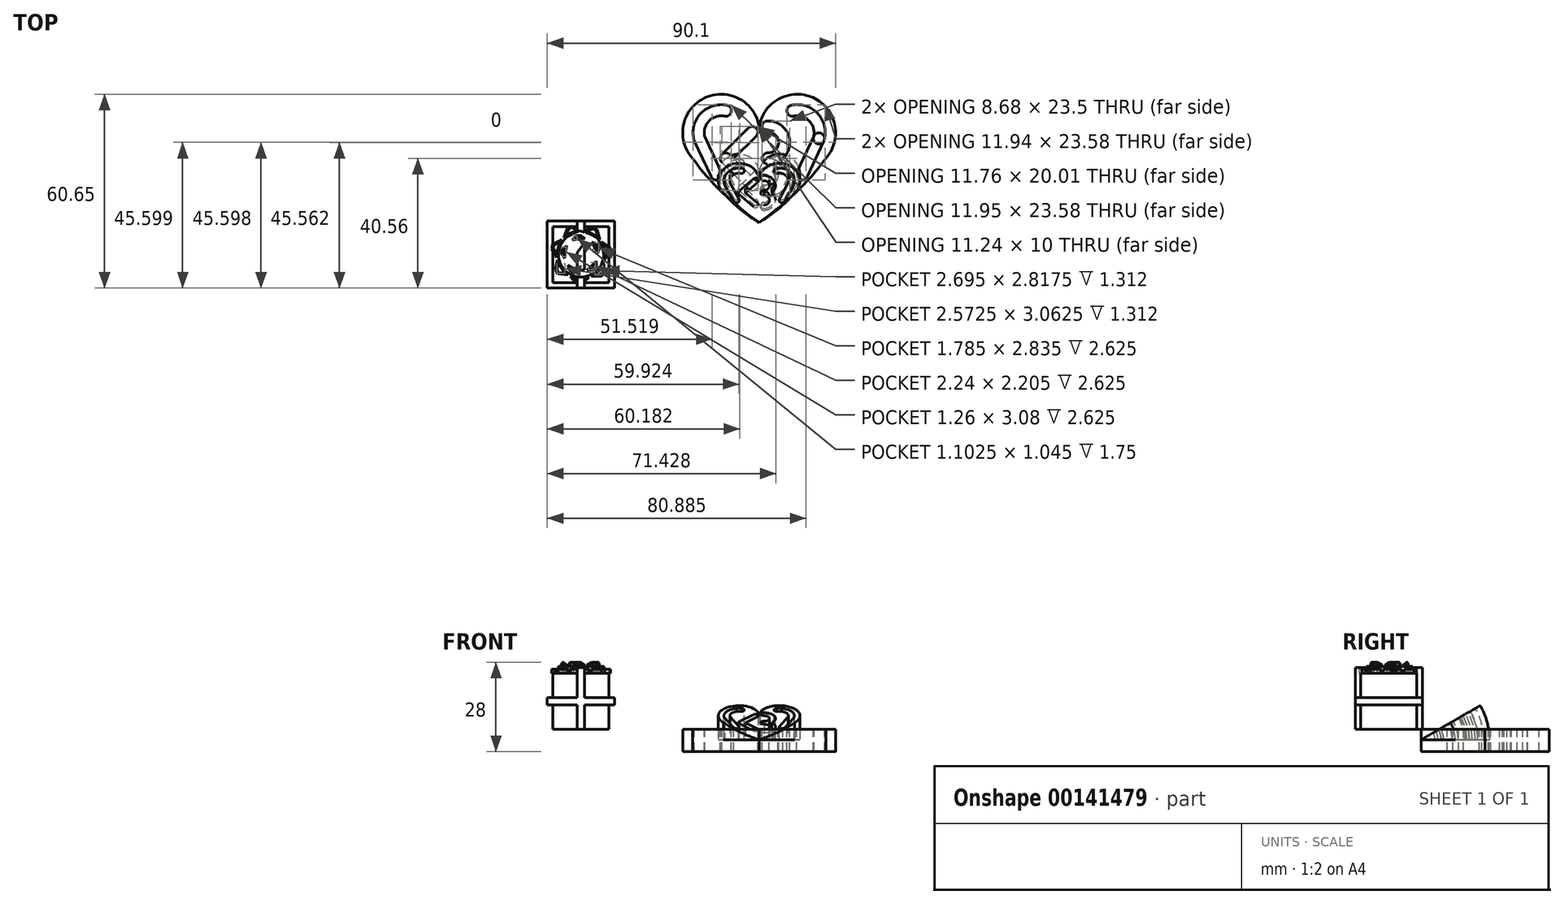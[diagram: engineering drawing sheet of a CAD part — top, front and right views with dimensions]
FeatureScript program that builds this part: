
annotation { "Feature Type Name" : "Feature", "Feature Type Description" : "" }
export const myFeature = defineFeature(function(context is Context, id is Id, definition is map)
    precondition{}
    {
        {
            var Q0;
            Q0=qCreatedBy(makeId("Top.planeOp"),FACE);
            var sketch = newSketch(context, id + "F0", { "sketchPlane" : qUnion([Q0])});
            skPoint(sketch, "E0", {"position": v(20.81, 20) * mm});
            skPoint(sketch, "E0.positionSnap0", {"position": v(0, 20) * mm});
            skPoint(sketch, "E0.positionSnap1", {"position": v(20.81, 40) * mm});
            skPoint(sketch, "E1", {"position": v(20.81, 30) * mm});
            skPoint(sketch, "E2", {"position": v(41.62, 20) * mm});
            skPoint(sketch, "E3", {"position": v(0, 30) * mm});
            skPoint(sketch, "E4", {"position": v(41.62, 30) * mm});
            skPoint(sketch, "E5", {"position": v(10.4, 40) * mm});
            skPoint(sketch, "E6", {"position": v(30.21, 39.83) * mm});
            skArc(sketch, "E7", {"start": v(20.81, 30) * mm, "mid": v(3.73, 38.9) * mm, "end": v(0, 20) * mm});
            skArc(sketch, "E8", {"start": v(0, 20) * mm, "mid": v(9.56, 9.12) * mm, "end": v(20.81, 0) * mm});
            skLineSegment(sketch, "E9.MirrorCS", {"start": v(20.81, 30) * mm, "end": v(20.81, 30) * mm});
            skArc(sketch, "E10.MirrorCS", {"start": v(41.62, 20) * mm, "mid": v(32.06, 9.12) * mm, "end": v(20.81, 0) * mm});
            skLineSegment(sketch, "E11.bottom", {"start": v(10.4, 30) * mm, "end": v(15.6, 30) * mm, "construction": true});
            skLineSegment(sketch, "E11.top", {"start": v(10.4, 10) * mm, "end": v(31.22, 10) * mm, "construction": true});
            skLineSegment(sketch, "E11.left", {"start": v(10.4, 30) * mm, "end": v(10.4, 20) * mm, "construction": true});
            skLineSegment(sketch, "E11.right", {"start": v(31.22, 30) * mm, "end": v(31.22, 20) * mm, "construction": true});
            skLineSegment(sketch, "E12", {"start": v(0, 20) * mm, "end": v(10.4, 20) * mm, "construction": true});
            skLineSegment(sketch, "E13", {"start": v(20.81, 30) * mm, "end": v(31.22, 30) * mm, "construction": true});
            skPoint(sketch, "E14", {"position": v(15.6, 30) * mm});
            skPoint(sketch, "E15", {"position": v(10.4, 20) * mm});
            skLineSegment(sketch, "E16", {"start": v(10.4, 20) * mm, "end": v(10.4, 10) * mm, "construction": true});
            skLineSegment(sketch, "E17", {"start": v(10.4, 20) * mm, "end": v(20.94, 20) * mm, "construction": true});
            skLineSegment(sketch, "E18", {"start": v(15.6, 30) * mm, "end": v(20.81, 30) * mm, "construction": true});
            skPoint(sketch, "E19", {"position": v(5.2, 20) * mm});
            skPoint(sketch, "E20", {"position": v(26.01, 30) * mm});
            skPoint(sketch, "E21", {"position": v(26.01, 20) * mm});
            skPoint(sketch, "E22", {"position": v(31.22, 20) * mm});
            skLineSegment(sketch, "E23", {"start": v(31.22, 20) * mm, "end": v(31.22, 15) * mm, "construction": true});
            skPoint(sketch, "E24", {"position": v(31.22, 25) * mm});
            skArc(sketch, "E25", {"start": v(23.45, 20) * mm, "mid": v(28.65, 25) * mm, "end": v(23.45, 30) * mm});
            skArc(sketch, "E26.MirrorCS", {"start": v(23.45, 20) * mm, "mid": v(28.65, 15) * mm, "end": v(23.45, 10) * mm});
            skLineSegment(sketch, "E27", {"start": v(20.94, 20) * mm, "end": v(26.01, 20) * mm, "construction": true});
            skLineSegment(sketch, "E28", {"start": v(26.01, 20) * mm, "end": v(41.62, 20) * mm, "construction": true});
            skPoint(sketch, "E29", {"position": v(23.48, 20) * mm});
            skPoint(sketch, "E30", {"position": v(18.21, 30) * mm});
            skArc(sketch, "E31.1.startCap", {"start": v(23.38, 18.25) * mm, "mid": v(21.7, 20.07) * mm, "end": v(23.52, 21.75) * mm});
            skArc(sketch, "E31.1.endCap", {"start": v(23.52, 28.25) * mm, "mid": v(21.7, 29.93) * mm, "end": v(23.38, 31.75) * mm});
            skArc(sketch, "E31.1.left", {"start": v(23.52, 21.75) * mm, "mid": v(26.9, 25) * mm, "end": v(23.52, 28.25) * mm});
            skArc(sketch, "E31.1.right", {"start": v(23.38, 18.25) * mm, "mid": v(30.4, 25) * mm, "end": v(23.38, 31.75) * mm});
            skArc(sketch, "E31.2.startCap", {"start": v(23.52, 18.25) * mm, "mid": v(21.7, 19.93) * mm, "end": v(23.38, 21.75) * mm});
            skArc(sketch, "E31.2.endCap", {"start": v(23.38, 8.25) * mm, "mid": v(21.7, 10.07) * mm, "end": v(23.52, 11.75) * mm});
            skArc(sketch, "E31.2.left", {"start": v(23.38, 21.75) * mm, "mid": v(30.4, 15) * mm, "end": v(23.38, 8.25) * mm});
            skArc(sketch, "E31.2.right", {"start": v(23.52, 18.25) * mm, "mid": v(26.9, 15) * mm, "end": v(23.52, 11.75) * mm});
            skLineSegment(sketch, "E32", {"start": v(0, 0) * mm, "end": v(75.27, 0) * mm, "construction": true});
            skPoint(sketch, "E33", {"position": v(20.81, 10) * mm});
            skPoint(sketch, "E34", {"position": v(20.81, 5) * mm});
            skPoint(sketch, "E35", {"position": v(17.47, 5) * mm});
            skPoint(sketch, "E36", {"position": v(24.15, 5) * mm});
            skLineSegment(sketch, "E37", {"start": v(17.47, 5) * mm, "end": v(24.15, 5) * mm, "construction": true});
            skArc(sketch, "E38", {"start": v(20.81, 30) * mm, "mid": v(23.99, 36.37) * mm, "end": v(30.21, 39.83) * mm});
            skArc(sketch, "E39", {"start": v(30.21, 39.83) * mm, "mid": v(41.4, 36.35) * mm, "end": v(44.32, 25) * mm});
            skLineSegment(sketch, "E40", {"start": v(31.22, 25) * mm, "end": v(46.35, 25) * mm, "construction": true});
            skArc(sketch, "E41", {"start": v(44.32, 25) * mm, "mid": v(43.27, 22.34) * mm, "end": v(41.62, 20) * mm});
            skArc(sketch, "E42.0", {"start": v(31.24, 34.94) * mm, "mid": v(37.78, 32.9) * mm, "end": v(39.49, 26.27) * mm});
            skLineSegment(sketch, "E43", {"start": v(31.22, 15) * mm, "end": v(31.22, 10) * mm, "construction": true});
            skLineSegment(sketch, "E44", {"start": v(39.49, 26.27) * mm, "end": v(34.24, 15) * mm});
            skArc(sketch, "E45.0.startCap", {"start": v(31.6, 33.23) * mm, "mid": v(29.53, 34.58) * mm, "end": v(30.88, 36.65) * mm});
            skArc(sketch, "E45.0.endCap", {"start": v(41.18, 25.83) * mm, "mid": v(39.04, 24.58) * mm, "end": v(37.8, 26.72) * mm});
            skArc(sketch, "E45.0.left", {"start": v(30.88, 36.65) * mm, "mid": v(39.05, 34.11) * mm, "end": v(41.18, 25.83) * mm});
            skArc(sketch, "E45.0.right", {"start": v(31.6, 33.23) * mm, "mid": v(36.51, 31.7) * mm, "end": v(37.8, 26.72) * mm});
            skArc(sketch, "E45.1.startCap", {"start": v(37.9, 27) * mm, "mid": v(40.23, 27.86) * mm, "end": v(41.08, 25.53) * mm});
            skArc(sketch, "E45.1.endCap", {"start": v(35.83, 14.26) * mm, "mid": v(33.5, 13.41) * mm, "end": v(32.66, 15.74) * mm});
            skLineSegment(sketch, "E45.1.left", {"start": v(41.08, 25.53) * mm, "end": v(35.83, 14.26) * mm});
            skLineSegment(sketch, "E45.1.right", {"start": v(37.9, 27) * mm, "end": v(32.66, 15.74) * mm});
            skLineSegment(sketch, "E46", {"start": v(20.81, 30) * mm, "end": v(20.81, 0) * mm, "construction": true});
            skLineSegment(sketch, "E47.MirrorCS", {"start": v(3.72, 27) * mm, "end": v(8.97, 15.74) * mm});
            skLineSegment(sketch, "E48.MirrorCS", {"start": v(2.13, 26.27) * mm, "end": v(7.38, 15) * mm});
            skArc(sketch, "E49.MirrorCS", {"start": v(5.8, 14.26) * mm, "mid": v(8.12, 13.41) * mm, "end": v(8.97, 15.74) * mm});
            skLineSegment(sketch, "E50.MirrorCS", {"start": v(0.55, 25.53) * mm, "end": v(5.8, 14.26) * mm});
            skArc(sketch, "E51.MirrorCS", {"start": v(3.72, 27) * mm, "mid": v(1.4, 27.86) * mm, "end": v(0.55, 25.53) * mm});
            skArc(sketch, "E52.MirrorCS", {"start": v(0.44, 25.83) * mm, "mid": v(2.58, 24.58) * mm, "end": v(3.83, 26.72) * mm});
            skArc(sketch, "E53.MirrorCS", {"start": v(10.74, 36.65) * mm, "mid": v(2.57, 34.11) * mm, "end": v(0.44, 25.83) * mm});
            skArc(sketch, "E54.MirrorCS", {"start": v(10.38, 34.94) * mm, "mid": v(3.84, 32.9) * mm, "end": v(2.13, 26.27) * mm});
            skArc(sketch, "E55.MirrorCS", {"start": v(10.02, 33.23) * mm, "mid": v(5.1, 31.7) * mm, "end": v(3.83, 26.72) * mm});
            skArc(sketch, "E56.MirrorCS", {"start": v(10.02, 33.23) * mm, "mid": v(12.1, 34.58) * mm, "end": v(10.74, 36.65) * mm});
            skLineSegment(sketch, "E57", {"start": v(10.4, 20) * mm, "end": v(18.66, 28.25) * mm});
            skLineSegment(sketch, "E58.MirrorCS", {"start": v(10.4, 20) * mm, "end": v(18.66, 11.75) * mm});
            skArc(sketch, "E59.0.startCap", {"start": v(11.64, 18.76) * mm, "mid": v(9.17, 18.76) * mm, "end": v(9.17, 21.24) * mm});
            skArc(sketch, "E59.0.endCap", {"start": v(17.42, 29.49) * mm, "mid": v(19.9, 29.49) * mm, "end": v(19.9, 27.01) * mm});
            skLineSegment(sketch, "E59.0.left", {"start": v(9.17, 21.24) * mm, "end": v(17.42, 29.49) * mm});
            skLineSegment(sketch, "E59.0.right", {"start": v(11.64, 18.76) * mm, "end": v(19.9, 27.01) * mm});
            skArc(sketch, "E59.1.startCap", {"start": v(9.17, 18.76) * mm, "mid": v(9.17, 21.24) * mm, "end": v(11.64, 21.24) * mm});
            skArc(sketch, "E59.1.endCap", {"start": v(19.9, 12.99) * mm, "mid": v(19.9, 10.51) * mm, "end": v(17.42, 10.51) * mm});
            skLineSegment(sketch, "E59.1.left", {"start": v(11.64, 21.24) * mm, "end": v(19.9, 12.99) * mm});
            skLineSegment(sketch, "E59.1.right", {"start": v(9.17, 18.76) * mm, "end": v(17.42, 10.51) * mm});
            skSolve(sketch);
        }
        {
            var Q0;
            Q0=makeQuery(id+"F0.imprint","IMPRINT",FACE,{"disambiguationData":[TD([[makeQuery(id+"F0.imprint","IMPRINT",EDGE,{"derivedFrom":sQuery(id+"F0.wireOp",EDGE,"E7")}),1.0]])]});
            var Q1;
            Q1=sQuery(id+"F0.wireOp",EDGE,"E32");
            revolve(context, id + "F1", {"entities" : qUnion([Q0]), "axis" : qUnion([Q1]), "revolveType" : RevolveType.ONE_DIRECTION, "angle" : (PI / 6) * radian});
        }
        {
            var Q0;
            Q0=makeQuery(id+"F1.opRevolve","CAP_FACE",FACE,{"disambiguationData":[OSD([sQuery(id+"F0.wireOp",EDGE,"E7"),sQuery(id+"F0.wireOp",EDGE,"E8"),sQuery(id+"F0.wireOp",EDGE,"E10.MirrorCS"),sQuery(id+"F0.wireOp",EDGE,"E31.1.endCap"),sQuery(id+"F0.wireOp",EDGE,"E31.1.left"),sQuery(id+"F0.wireOp",EDGE,"E31.1.right"),sQuery(id+"F0.wireOp",EDGE,"E31.2.startCap"),sQuery(id+"F0.wireOp",EDGE,"E31.2.endCap"),sQuery(id+"F0.wireOp",EDGE,"E31.2.left"),sQuery(id+"F0.wireOp",EDGE,"E31.2.right"),sQuery(id+"F0.wireOp",EDGE,"E38"),sQuery(id+"F0.wireOp",EDGE,"E39"),sQuery(id+"F0.wireOp",EDGE,"E41"),sQuery(id+"F0.wireOp",EDGE,"E45.0.startCap"),sQuery(id+"F0.wireOp",EDGE,"E45.0.left"),sQuery(id+"F0.wireOp",EDGE,"E45.0.right"),sQuery(id+"F0.wireOp",EDGE,"E45.1.startCap"),sQuery(id+"F0.wireOp",EDGE,"E45.1.endCap"),sQuery(id+"F0.wireOp",EDGE,"E45.1.left"),sQuery(id+"F0.wireOp",EDGE,"E45.1.right"),sQuery(id+"F0.wireOp",EDGE,"E47.MirrorCS"),sQuery(id+"F0.wireOp",EDGE,"E49.MirrorCS"),sQuery(id+"F0.wireOp",EDGE,"E50.MirrorCS"),sQuery(id+"F0.wireOp",EDGE,"E52.MirrorCS"),sQuery(id+"F0.wireOp",EDGE,"E53.MirrorCS"),sQuery(id+"F0.wireOp",EDGE,"E55.MirrorCS"),sQuery(id+"F0.wireOp",EDGE,"E56.MirrorCS"),sQuery(id+"F0.wireOp",EDGE,"E59.0.endCap"),sQuery(id+"F0.wireOp",EDGE,"E59.0.left"),sQuery(id+"F0.wireOp",EDGE,"E59.0.right"),sQuery(id+"F0.wireOp",EDGE,"E59.1.startCap"),sQuery(id+"F0.wireOp",EDGE,"E59.1.endCap"),sQuery(id+"F0.wireOp",EDGE,"E59.1.left"),sQuery(id+"F0.wireOp",EDGE,"E59.1.right")])],"isStart":true});
            var Q1;
            {var subQ0=sQuery(id+"F0.wireOp",EDGE,"E53.MirrorCS");Q1=makeQuery(id+"F0.imprint","IMPRINT",FACE,{"disambiguationData":[TD([[makeQuery(id+"F0.imprint","IMPRINT",EDGE,{"derivedFrom":subQ0}),1.0]])]});}
            var Q2;
            {var subQ3=sQuery(id+"F0.wireOp",EDGE,"E49.MirrorCS");Q2=makeQuery(id+"F0.imprint","IMPRINT",FACE,{"disambiguationData":[TD([[makeQuery(id+"F0.imprint","IMPRINT",EDGE,{"derivedFrom":subQ3}),1.0]])]});}
            var Q3;
            {var subQ2=sQuery(id+"F0.wireOp",EDGE,"E48.MirrorCS");var subQ6=sQuery(id+"F0.wireOp",EDGE,"E54.MirrorCS");var subQ8=makeQuery(id+"F0.imprint","INTERSECT",VERTEX,{"derivedFrom":[subQ2,subQ6]});Q3=makeQuery(id+"F0.imprint","IMPRINT",FACE,{"disambiguationData":[TD([[makeQuery(id+"F0.imprint","IMPRINT",EDGE,{"disambiguationData":[TD([[subQ8,-1.0]])],"derivedFrom":subQ2}),-1.0]])]});}
            var Q4;
            {var subQ0=sQuery(id+"F0.wireOp",EDGE,"E45.1.endCap");Q4=makeQuery(id+"F0.imprint","IMPRINT",FACE,{"disambiguationData":[TD([[makeQuery(id+"F0.imprint","IMPRINT",EDGE,{"derivedFrom":subQ0}),-1.0]])]});}
            var Q5;
            {var subQ2=sQuery(id+"F0.wireOp",EDGE,"E42.0");var subQ6=sQuery(id+"F0.wireOp",EDGE,"E44");var subQ8=makeQuery(id+"F0.imprint","INTERSECT",VERTEX,{"derivedFrom":[subQ2,subQ6]});Q5=makeQuery(id+"F0.imprint","IMPRINT",FACE,{"disambiguationData":[TD([[makeQuery(id+"F0.imprint","IMPRINT",EDGE,{"disambiguationData":[TD([[subQ8,1.0]])],"derivedFrom":subQ2}),1.0]])]});}
            var Q6;
            {var subQ5=sQuery(id+"F0.wireOp",EDGE,"E45.0.startCap");Q6=makeQuery(id+"F0.imprint","IMPRINT",FACE,{"disambiguationData":[TD([[makeQuery(id+"F0.imprint","IMPRINT",EDGE,{"derivedFrom":subQ5}),-1.0]])]});}
            var Q7;
            {var subQ5=sQuery(id+"F0.wireOp",EDGE,"E44");var subQ7=sQuery(id+"F0.wireOp",EDGE,"E42.0");var subQ8=makeQuery(id+"F0.imprint","INTERSECT",VERTEX,{"derivedFrom":[subQ7,subQ5]});Q7=makeQuery(id+"F0.imprint","IMPRINT",FACE,{"disambiguationData":[TD([[makeQuery(id+"F0.imprint","IMPRINT",EDGE,{"disambiguationData":[TD([[subQ8,1.0]])],"derivedFrom":subQ7}),-1.0]])]});}
            var Q8;
            {var subQ7=sQuery(id+"F0.wireOp",EDGE,"E47.MirrorCS");var subQ9=sQuery(id+"F0.wireOp",EDGE,"E51.MirrorCS");var subQ10=makeQuery(id+"F0.imprint","INTERSECT",VERTEX,{"derivedFrom":[subQ7,subQ9]});Q8=makeQuery(id+"F0.imprint","IMPRINT",FACE,{"disambiguationData":[TD([[makeQuery(id+"F0.imprint","IMPRINT",EDGE,{"disambiguationData":[TD([[subQ10,-1.0]])],"derivedFrom":subQ7}),-1.0]])]});}
            var Q9;
            {var subQ0=sQuery(id+"F0.wireOp",EDGE,"E58.MirrorCS");var subQ1=sQuery(id+"F0.wireOp",EDGE,"E57");var subQ2=makeQuery(id+"F0.imprint","INTERSECT",VERTEX,{"derivedFrom":[subQ1,subQ0]});Q9=makeQuery(id+"F0.imprint","IMPRINT",FACE,{"disambiguationData":[TD([[makeQuery(id+"F0.imprint","IMPRINT",EDGE,{"disambiguationData":[TD([[subQ2,-1.0]])],"derivedFrom":subQ1}),-1.0]])]});}
            var Q10;
            {var subQ1=sQuery(id+"F0.wireOp",EDGE,"E59.0.startCap");Q10=makeQuery(id+"F0.imprint","IMPRINT",FACE,{"disambiguationData":[TD([[makeQuery(id+"F0.imprint","IMPRINT",EDGE,{"derivedFrom":subQ1}),-1.0]])]});}
            var Q11;
            {var subQ1=sQuery(id+"F0.wireOp",EDGE,"E59.0.endCap");Q11=makeQuery(id+"F0.imprint","IMPRINT",FACE,{"disambiguationData":[TD([[makeQuery(id+"F0.imprint","IMPRINT",EDGE,{"derivedFrom":subQ1}),-1.0]])]});}
            var Q12;
            {var subQ4=sQuery(id+"F0.wireOp",EDGE,"E59.0.startCap");Q12=makeQuery(id+"F0.imprint","IMPRINT",FACE,{"disambiguationData":[TD([[makeQuery(id+"F0.imprint","IMPRINT",EDGE,{"derivedFrom":subQ4}),1.0]])]});}
            var Q13;
            {var subQ1=sQuery(id+"F0.wireOp",EDGE,"E31.2.endCap");Q13=makeQuery(id+"F0.imprint","IMPRINT",FACE,{"disambiguationData":[TD([[makeQuery(id+"F0.imprint","IMPRINT",EDGE,{"derivedFrom":subQ1}),-1.0]])]});}
            var Q14;
            {var subQ4=sQuery(id+"F0.wireOp",EDGE,"E31.1.endCap");Q14=makeQuery(id+"F0.imprint","IMPRINT",FACE,{"disambiguationData":[TD([[makeQuery(id+"F0.imprint","IMPRINT",EDGE,{"derivedFrom":subQ4}),-1.0]])]});}
            var Q15;
            {var subQ0=sQuery(id+"F0.wireOp",EDGE,"E26.MirrorCS");var subQ1=sQuery(id+"F0.wireOp",EDGE,"E25");var subQ2=makeQuery(id+"F0.imprint","INTERSECT",VERTEX,{"disambiguationData":[OD(1.0)],"derivedFrom":[subQ1,subQ0]});Q15=makeQuery(id+"F0.imprint","IMPRINT",FACE,{"disambiguationData":[TD([[makeQuery(id+"F0.imprint","IMPRINT",EDGE,{"disambiguationData":[TD([[subQ2,-1.0]])],"derivedFrom":subQ1}),-1.0]])]});}
            var Q16;
            {var subQ10=sQuery(id+"F0.wireOp",EDGE,"E31.1.startCap");Q16=makeQuery(id+"F0.imprint","IMPRINT",FACE,{"disambiguationData":[TD([[makeQuery(id+"F0.imprint","IMPRINT",EDGE,{"derivedFrom":subQ10}),-1.0]])]});}
            extrude(context, id + "F2", {"entities" : qUnion([Q0, Q1, Q2, Q3, Q4, Q5, Q6, Q7, Q8, Q9, Q10, Q11, Q12, Q13, Q14, Q15, Q16]), "operationType" : NewBodyOperationType.ADD, "depth" : 7 * mm});
        }
        {
            var Q0;
            Q0=makeQuery(id+"F1.opRevolve","SWEPT_BODY",BODY,{"disambiguationData":[OSD([sQuery(id+"F0.wireOp",EDGE,"E7"),sQuery(id+"F0.wireOp",EDGE,"E8"),sQuery(id+"F0.wireOp",EDGE,"E10.MirrorCS"),sQuery(id+"F0.wireOp",EDGE,"E31.1.endCap"),sQuery(id+"F0.wireOp",EDGE,"E31.1.left"),sQuery(id+"F0.wireOp",EDGE,"E31.1.right"),sQuery(id+"F0.wireOp",EDGE,"E31.2.startCap"),sQuery(id+"F0.wireOp",EDGE,"E31.2.endCap"),sQuery(id+"F0.wireOp",EDGE,"E31.2.left"),sQuery(id+"F0.wireOp",EDGE,"E31.2.right"),sQuery(id+"F0.wireOp",EDGE,"E38"),sQuery(id+"F0.wireOp",EDGE,"E39"),sQuery(id+"F0.wireOp",EDGE,"E41"),sQuery(id+"F0.wireOp",EDGE,"E45.0.startCap"),sQuery(id+"F0.wireOp",EDGE,"E45.0.left"),sQuery(id+"F0.wireOp",EDGE,"E45.0.right"),sQuery(id+"F0.wireOp",EDGE,"E45.1.startCap"),sQuery(id+"F0.wireOp",EDGE,"E45.1.endCap"),sQuery(id+"F0.wireOp",EDGE,"E45.1.left"),sQuery(id+"F0.wireOp",EDGE,"E45.1.right"),sQuery(id+"F0.wireOp",EDGE,"E47.MirrorCS"),sQuery(id+"F0.wireOp",EDGE,"E49.MirrorCS"),sQuery(id+"F0.wireOp",EDGE,"E50.MirrorCS"),sQuery(id+"F0.wireOp",EDGE,"E52.MirrorCS"),sQuery(id+"F0.wireOp",EDGE,"E53.MirrorCS"),sQuery(id+"F0.wireOp",EDGE,"E55.MirrorCS"),sQuery(id+"F0.wireOp",EDGE,"E56.MirrorCS"),sQuery(id+"F0.wireOp",EDGE,"E59.0.endCap"),sQuery(id+"F0.wireOp",EDGE,"E59.0.left"),sQuery(id+"F0.wireOp",EDGE,"E59.0.right"),sQuery(id+"F0.wireOp",EDGE,"E59.1.startCap"),sQuery(id+"F0.wireOp",EDGE,"E59.1.endCap"),sQuery(id+"F0.wireOp",EDGE,"E59.1.left"),sQuery(id+"F0.wireOp",EDGE,"E59.1.right")])]});
            var Q1;
            Q1=makeQuery(id+"F2.opExtrude","CAP_VERTEX",VERTEX,{"disambiguationData":[OSD([sQuery(id+"F0.wireOp",EDGE,"E8"),sQuery(id+"F0.wireOp",EDGE,"E10.MirrorCS")])],"isStart":false});
            transform(context, id + "F3", {"entities" : qUnion([Q0]), "transformType" : TransformType.SCALE_UNIFORMLY, "scale" : 1 / 3, "scalePoint" : qUnion([Q1]), "makeCopy" : false});
        }
        {
            var Q0;
            Q0=qCreatedBy(makeId("Top.planeOp"),FACE);
            var sketch = newSketch(context, id + "F4", { "sketchPlane" : qUnion([Q0])});
            skLineSegment(sketch, "E60.bottom", {"start": v(-43.64, -8.81) * mm, "end": v(-33.64, -8.81) * mm});
            skLineSegment(sketch, "E60.top", {"start": v(-43.64, -18.81) * mm, "end": v(-33.64, -18.81) * mm});
            skLineSegment(sketch, "E60.left", {"start": v(-43.64, -8.81) * mm, "end": v(-43.64, -18.81) * mm});
            skLineSegment(sketch, "E60.right", {"start": v(-33.64, -8.81) * mm, "end": v(-33.64, -18.81) * mm});
            skSolve(sketch);
        }
        {
            var Q0;
            Q0=makeQuery(id+"F4.imprint","IMPRINT",FACE,{"disambiguationData":[TD([[makeQuery(id+"F4.imprint","IMPRINT",EDGE,{"derivedFrom":sQuery(id+"F4.wireOp",EDGE,"E60.bottom")}),-1.0]])]});
            extrude(context, id + "F5", {"entities" : qUnion([Q0]), "depth" : 10 * mm});
        }
        {
            var Q0;
            Q0=makeQuery(id+"F5.opExtrude","SWEPT_FACE",FACE,{"disambiguationData":[OSD([sQuery(id+"F4.wireOp",EDGE,"E60.top")])]});
            var sketch = newSketch(context, id + "F6", { "sketchPlane" : qUnion([Q0])});
            skPoint(sketch, "E61", {"position": v(-43.64, 5) * mm});
            skPoint(sketch, "E62", {"position": v(-38.64, 10) * mm});
            skLineSegment(sketch, "E63", {"start": v(-43.64, 10) * mm, "end": v(-33.64, 10) * mm, "construction": true});
            skLineSegment(sketch, "E64", {"start": v(-43.64, 10) * mm, "end": v(-43.64, 0) * mm, "construction": true});
            skPoint(sketch, "E65", {"position": v(-43.64, 5.67) * mm});
            skLineSegment(sketch, "E66", {"start": v(-43.64, 5) * mm, "end": v(-33.64, 5) * mm, "construction": true});
            skLineSegment(sketch, "E67", {"start": v(-38.64, 10) * mm, "end": v(-38.64, 0) * mm, "construction": true});
            skLineSegment(sketch, "E68", {"start": v(-43.64, 5.67) * mm, "end": v(-33.64, 5.67) * mm});
            skLineSegment(sketch, "E69.MirrorCS", {"start": v(-43.64, 4.33) * mm, "end": v(-33.64, 4.33) * mm});
            skLineSegment(sketch, "E70", {"start": v(-39.31, 10) * mm, "end": v(-39.31, 0) * mm});
            skLineSegment(sketch, "E71.MirrorCS", {"start": v(-37.98, 10) * mm, "end": v(-37.98, 0) * mm});
            skSolve(sketch);
        }
        {
            var Q0;
            Q0 = qSketchRegion(id + "F6", true);
            var Q1;
            {var subQ0=sQuery(id+"F6.wireOp",EDGE,"E70");var subQ1=sQuery(id+"F6.wireOp",EDGE,"E68");var subQ2=makeQuery(id+"F6.imprint","INTERSECT",VERTEX,{"derivedFrom":[subQ1,subQ0]});Q1=makeQuery(id+"F6.imprint","IMPRINT",FACE,{"disambiguationData":[TD([[makeQuery(id+"F6.imprint","IMPRINT",EDGE,{"disambiguationData":[TD([[subQ2,-1.0]])],"derivedFrom":subQ1}),1.0]])]});}
            var Q2;
            {var subQ0=sQuery(id+"F6.wireOp",EDGE,"E68");var subQ3=sQuery(id+"F6.wireOp",EDGE,"E70");var subQ4=makeQuery(id+"F6.imprint","INTERSECT",VERTEX,{"derivedFrom":[subQ0,subQ3]});Q2=makeQuery(id+"F6.imprint","IMPRINT",FACE,{"disambiguationData":[TD([[makeQuery(id+"F6.imprint","IMPRINT",EDGE,{"disambiguationData":[TD([[subQ4,-1.0]])],"derivedFrom":subQ3}),-1.0]])]});}
            var Q3;
            {var subQ0=sQuery(id+"F6.wireOp",EDGE,"E68");var subQ3=sQuery(id+"F6.wireOp",EDGE,"E71.MirrorCS");var subQ4=makeQuery(id+"F6.imprint","INTERSECT",VERTEX,{"derivedFrom":[subQ0,subQ3]});Q3=makeQuery(id+"F6.imprint","IMPRINT",FACE,{"disambiguationData":[TD([[makeQuery(id+"F6.imprint","IMPRINT",EDGE,{"disambiguationData":[TD([[subQ4,-1.0]])],"derivedFrom":subQ3}),1.0]])]});}
            var Q4;
            {var subQ0=sQuery(id+"F6.wireOp",EDGE,"E70");var subQ1=sQuery(id+"F6.wireOp",EDGE,"E69.MirrorCS");var subQ2=makeQuery(id+"F6.imprint","INTERSECT",VERTEX,{"derivedFrom":[subQ1,subQ0]});Q4=makeQuery(id+"F6.imprint","IMPRINT",FACE,{"disambiguationData":[TD([[makeQuery(id+"F6.imprint","IMPRINT",EDGE,{"disambiguationData":[TD([[subQ2,-1.0]])],"derivedFrom":subQ1}),-1.0]])]});}
            extrude(context, id + "F7", {"entities" : qUnion([Q0, Q1, Q2, Q3, Q4]), "operationType" : NewBodyOperationType.ADD, "depth" : 1 * mm});
        }
        {
            var Q0;
            {var subQ0=sQuery(id+"F4.wireOp",EDGE,"E60.left");Q0=makeQuery(id+"F7.boolean.opBoolean","MERGE",FACE,{"derivedFrom":[makeQuery(id+"F5.opExtrude","SWEPT_FACE",FACE,{"disambiguationData":[OSD([subQ0])]}),makeQuery(id+"F7.opExtrude","SWEPT_FACE",FACE,{"disambiguationData":[OSD([sQuery(id+"F4.wireOp",EDGE,"E60.top"),subQ0])]})]});}
            var sketch = newSketch(context, id + "F8", { "sketchPlane" : qUnion([Q0])});
            skLineSegment(sketch, "E72", {"start": v(19.81, 4.33) * mm, "end": v(8.81, 4.33) * mm});
            skLineSegment(sketch, "E73", {"start": v(19.81, 5.67) * mm, "end": v(8.81, 5.67) * mm});
            skSolve(sketch);
        }
        {
            var Q0;
            {var subQ1=sQuery(id+"F4.wireOp",EDGE,"E60.left");var subQ2=sQuery(id+"F4.wireOp",EDGE,"E60.top");var subQ3=makeQuery(id+"F7.opExtrude","CAP_EDGE",EDGE,{"disambiguationData":[OSD([subQ2,subQ1])],"isStart":false});Q0=makeQuery(id+"F8.imprint","IMPRINT",FACE,{"disambiguationData":[TD([[makeQuery(id+"F8.imprint","IMPRINT",EDGE,{"derivedFrom":subQ3}),-1.0]])]});}
            extrude(context, id + "F9", {"entities" : qUnion([Q0]), "operationType" : NewBodyOperationType.ADD, "depth" : 1 * mm});
        }
        {
            var Q0;
            {var subQ0=sQuery(id+"F4.wireOp",EDGE,"E60.right");Q0=makeQuery(id+"F7.boolean.opBoolean","MERGE",FACE,{"derivedFrom":[makeQuery(id+"F5.opExtrude","SWEPT_FACE",FACE,{"disambiguationData":[OSD([subQ0])]}),makeQuery(id+"F7.opExtrude","SWEPT_FACE",FACE,{"disambiguationData":[OSD([sQuery(id+"F4.wireOp",EDGE,"E60.top"),subQ0])]})]});}
            var sketch = newSketch(context, id + "F10", { "sketchPlane" : qUnion([Q0])});
            skLineSegment(sketch, "E74", {"start": v(-19.81, 4.33) * mm, "end": v(-8.81, 4.33) * mm});
            skLineSegment(sketch, "E75", {"start": v(-19.81, 5.67) * mm, "end": v(-8.81, 5.67) * mm});
            skSolve(sketch);
        }
        {
            var Q0;
            {var subQ1=sQuery(id+"F4.wireOp",EDGE,"E60.right");var subQ2=sQuery(id+"F4.wireOp",EDGE,"E60.top");var subQ3=makeQuery(id+"F7.opExtrude","CAP_EDGE",EDGE,{"disambiguationData":[OSD([subQ2,subQ1])],"isStart":false});Q0=makeQuery(id+"F10.imprint","IMPRINT",FACE,{"disambiguationData":[TD([[makeQuery(id+"F10.imprint","IMPRINT",EDGE,{"derivedFrom":subQ3}),1.0]])]});}
            extrude(context, id + "F11", {"entities" : qUnion([Q0]), "operationType" : NewBodyOperationType.ADD, "depth" : 1 * mm});
        }
        {
            var Q0;
            {var subQ0=sQuery(id+"F4.wireOp",EDGE,"E60.top");var subQ1=makeQuery(id+"F5.opExtrude","CAP_EDGE",EDGE,{"disambiguationData":[OSD([subQ0])],"isStart":false});Q0=makeQuery(id+"F7.boolean.opBoolean","MERGE",FACE,{"derivedFrom":[makeQuery(id+"F5.opExtrude","CAP_FACE",FACE,{"disambiguationData":[OSD([sQuery(id+"F4.wireOp",EDGE,"E60.bottom"),subQ0,sQuery(id+"F4.wireOp",EDGE,"E60.left"),sQuery(id+"F4.wireOp",EDGE,"E60.right")])],"isStart":false}),makeQuery(id+"F7.opExtrude","SWEPT_FACE",FACE,{"disambiguationData":[OSD([subQ0]),TDD([makeQuery(id+"F6.imprint","IMPRINT",EDGE,{"disambiguationData":[TD([[makeQuery(id+"F6.imprint","INTERSECT",VERTEX,{"derivedFrom":[subQ1,sQuery(id+"F6.wireOp",EDGE,"E70")]}),-1.0]])],"derivedFrom":subQ1})])]})]});}
            var sketch = newSketch(context, id + "F12", { "sketchPlane" : qUnion([Q0])});
            skLineSegment(sketch, "E76", {"start": v(-37.98, -19.81) * mm, "end": v(-37.98, -8.81) * mm});
            skPoint(sketch, "E76.endSnap0", {"position": v(-37.98, -19.31) * mm});
            skLineSegment(sketch, "E77", {"start": v(-39.31, -19.81) * mm, "end": v(-39.31, -8.81) * mm});
            skLineSegment(sketch, "E78", {"start": v(-43.64, -8.81) * mm, "end": v(-43.64, -18.81) * mm, "construction": true});
            skLineSegment(sketch, "E79", {"start": v(-43.64, -18.81) * mm, "end": v(-33.64, -18.81) * mm, "construction": true});
            skLineSegment(sketch, "E80", {"start": v(-33.64, -18.81) * mm, "end": v(-33.64, -8.81) * mm, "construction": true});
            skLineSegment(sketch, "E81", {"start": v(-33.64, -8.81) * mm, "end": v(-43.64, -8.81) * mm, "construction": true});
            skPoint(sketch, "E82", {"position": v(-38.64, -13.81) * mm});
            skPoint(sketch, "E82.positionSnap0", {"position": v(-43.64, -13.81) * mm});
            skPoint(sketch, "E82.positionSnap1", {"position": v(-38.64, -8.81) * mm});
            skCircle(sketch, "E83.cCircle", {"center": v(-38.64, -13.81) * mm, "radius": 4 * mm});
            skLineSegment(sketch, "E83.0", {"start": v(-42.03, -11.12) * mm, "end": v(-39.13, -9.51) * mm});
            skLineSegment(sketch, "E83.1", {"start": v(-39.13, -9.51) * mm, "end": v(-35.95, -10.43) * mm});
            skLineSegment(sketch, "E83.2", {"start": v(-35.95, -10.43) * mm, "end": v(-34.34, -13.33) * mm});
            skLineSegment(sketch, "E83.3", {"start": v(-34.34, -13.33) * mm, "end": v(-35.26, -16.51) * mm});
            skLineSegment(sketch, "E83.4", {"start": v(-35.26, -16.51) * mm, "end": v(-38.16, -18.12) * mm});
            skLineSegment(sketch, "E83.5", {"start": v(-38.16, -18.12) * mm, "end": v(-41.34, -17.2) * mm});
            skLineSegment(sketch, "E83.6", {"start": v(-41.34, -17.2) * mm, "end": v(-42.95, -14.3) * mm});
            skLineSegment(sketch, "E83.7", {"start": v(-42.95, -14.3) * mm, "end": v(-42.03, -11.12) * mm});
            skPoint(sketch, "E83.0.midPoint", {"position": v(-40.58, -10.31) * mm});
            skLineSegment(sketch, "E84", {"start": v(-42.49, -12.7) * mm, "end": v(-44.17, -12.22) * mm, "construction": true});
            skLineSegment(sketch, "E85", {"start": v(-44.17, -12.22) * mm, "end": v(-43.88, -12.72) * mm, "construction": true});
            skLineSegment(sketch, "E86", {"start": v(-44.17, -12.22) * mm, "end": v(-43.66, -11.96) * mm, "construction": true});
            skPoint(sketch, "E87", {"position": v(-43.77, -12.34) * mm});
            skLineSegment(sketch, "E88", {"start": v(-43.77, -12.34) * mm, "end": v(-43.77, -12.34) * mm});
            skLineSegment(sketch, "E89", {"start": v(-43.77, -12.34) * mm, "end": v(-43.66, -11.96) * mm});
            skLineSegment(sketch, "E90", {"start": v(-43.66, -11.96) * mm, "end": v(-42.03, -11.12) * mm});
            skLineSegment(sketch, "E91", {"start": v(-43.88, -12.72) * mm, "end": v(-42.95, -14.3) * mm});
            skLineSegment(sketch, "E92", {"start": v(-43.77, -12.34) * mm, "end": v(-43.88, -12.72) * mm});
            skLineSegment(sketch, "E93.0", {"start": v(-43.03, -13.67) * mm, "end": v(-42.43, -11.6) * mm});
            skLineSegment(sketch, "E93.1", {"start": v(-43.45, -12.13) * mm, "end": v(-42.43, -11.6) * mm});
            skLineSegment(sketch, "E93.2", {"start": v(-43.6, -12.68) * mm, "end": v(-43.03, -13.67) * mm});
            skLineSegment(sketch, "E93.3", {"start": v(-43.53, -12.4) * mm, "end": v(-43.6, -12.68) * mm});
            skLineSegment(sketch, "E93.4", {"start": v(-43.53, -12.4) * mm, "end": v(-43.45, -12.13) * mm});
            skLineSegment(sketch, "E94.1.0", {"start": v(-42.62, -17) * mm, "end": v(-41.49, -17.15) * mm});
            skLineSegment(sketch, "E94.1.1", {"start": v(-41.49, -17.15) * mm, "end": v(-42.73, -15.4) * mm});
            skLineSegment(sketch, "E94.1.2", {"start": v(-42.79, -16.76) * mm, "end": v(-42.96, -16.52) * mm});
            skLineSegment(sketch, "E94.1.3", {"start": v(-42.79, -16.76) * mm, "end": v(-42.62, -17) * mm});
            skLineSegment(sketch, "E94.1.4", {"start": v(-43, -16.9) * mm, "end": v(-43.22, -16.58) * mm});
            skLineSegment(sketch, "E94.1.5", {"start": v(-43, -16.9) * mm, "end": v(-42.76, -17.22) * mm});
            skLineSegment(sketch, "E94.1.6", {"start": v(-43.22, -16.58) * mm, "end": v(-42.87, -14.78) * mm});
            skLineSegment(sketch, "E94.1.7", {"start": v(-42.96, -16.52) * mm, "end": v(-42.73, -15.4) * mm});
            skLineSegment(sketch, "E94.1.8", {"start": v(-40.95, -17.48) * mm, "end": v(-42.87, -14.78) * mm});
            skLineSegment(sketch, "E94.1.9", {"start": v(-42.76, -17.22) * mm, "end": v(-40.95, -17.48) * mm});
            skLineSegment(sketch, "E94.2.0", {"start": v(-38.64, -18.9) * mm, "end": v(-37.8, -18.12) * mm});
            skLineSegment(sketch, "E94.2.1", {"start": v(-37.8, -18.12) * mm, "end": v(-39.96, -18) * mm});
            skLineSegment(sketch, "E94.2.2", {"start": v(-38.93, -18.89) * mm, "end": v(-39.21, -18.87) * mm});
            skLineSegment(sketch, "E94.2.3", {"start": v(-38.93, -18.89) * mm, "end": v(-38.64, -18.9) * mm});
            skLineSegment(sketch, "E94.2.4", {"start": v(-38.94, -19.14) * mm, "end": v(-39.34, -19.12) * mm});
            skLineSegment(sketch, "E94.2.5", {"start": v(-38.94, -19.14) * mm, "end": v(-38.55, -19.16) * mm});
            skLineSegment(sketch, "E94.2.6", {"start": v(-39.34, -19.12) * mm, "end": v(-40.52, -17.72) * mm});
            skLineSegment(sketch, "E94.2.7", {"start": v(-39.21, -18.87) * mm, "end": v(-39.96, -18) * mm});
            skLineSegment(sketch, "E94.2.8", {"start": v(-37.21, -17.9) * mm, "end": v(-40.52, -17.72) * mm});
            skLineSegment(sketch, "E94.2.9", {"start": v(-38.55, -19.16) * mm, "end": v(-37.21, -17.9) * mm});
            skLineSegment(sketch, "E94.3.0", {"start": v(-34.66, -16.99) * mm, "end": v(-34.76, -15.84) * mm});
            skLineSegment(sketch, "E94.3.1", {"start": v(-34.76, -15.84) * mm, "end": v(-36.2, -17.45) * mm});
            skLineSegment(sketch, "E94.3.2", {"start": v(-34.85, -17.2) * mm, "end": v(-35.04, -17.41) * mm});
            skLineSegment(sketch, "E94.3.3", {"start": v(-34.85, -17.2) * mm, "end": v(-34.66, -16.99) * mm});
            skLineSegment(sketch, "E94.3.4", {"start": v(-34.67, -17.37) * mm, "end": v(-34.93, -17.66) * mm});
            skLineSegment(sketch, "E94.3.5", {"start": v(-34.67, -17.37) * mm, "end": v(-34.4, -17.07) * mm});
            skLineSegment(sketch, "E94.3.6", {"start": v(-34.93, -17.66) * mm, "end": v(-36.76, -17.71) * mm});
            skLineSegment(sketch, "E94.3.7", {"start": v(-35.04, -17.41) * mm, "end": v(-36.2, -17.45) * mm});
            skLineSegment(sketch, "E94.3.8", {"start": v(-34.56, -15.24) * mm, "end": v(-36.76, -17.71) * mm});
            skLineSegment(sketch, "E94.3.9", {"start": v(-34.4, -17.07) * mm, "end": v(-34.56, -15.24) * mm});
            skLineSegment(sketch, "E94.4.0", {"start": v(-33.68, -12.68) * mm, "end": v(-34.64, -12.04) * mm});
            skLineSegment(sketch, "E94.4.1", {"start": v(-34.64, -12.04) * mm, "end": v(-34.27, -14.16) * mm});
            skLineSegment(sketch, "E94.4.2", {"start": v(-33.63, -12.96) * mm, "end": v(-33.59, -13.24) * mm});
            skLineSegment(sketch, "E94.4.3", {"start": v(-33.63, -12.96) * mm, "end": v(-33.68, -12.68) * mm});
            skLineSegment(sketch, "E94.4.4", {"start": v(-33.39, -12.92) * mm, "end": v(-33.32, -13.3) * mm});
            skLineSegment(sketch, "E94.4.5", {"start": v(-33.39, -12.92) * mm, "end": v(-33.45, -12.53) * mm});
            skLineSegment(sketch, "E94.4.6", {"start": v(-33.32, -13.3) * mm, "end": v(-34.42, -14.78) * mm});
            skLineSegment(sketch, "E94.4.7", {"start": v(-33.59, -13.24) * mm, "end": v(-34.27, -14.16) * mm});
            skLineSegment(sketch, "E94.4.8", {"start": v(-34.98, -11.5) * mm, "end": v(-34.42, -14.78) * mm});
            skLineSegment(sketch, "E94.4.9", {"start": v(-33.45, -12.53) * mm, "end": v(-34.98, -11.5) * mm});
            skLineSegment(sketch, "E94.5.0", {"start": v(-36.44, -9.23) * mm, "end": v(-37.53, -9.57) * mm});
            skLineSegment(sketch, "E94.5.1", {"start": v(-37.53, -9.57) * mm, "end": v(-35.65, -10.61) * mm});
            skLineSegment(sketch, "E94.5.2", {"start": v(-36.19, -9.36) * mm, "end": v(-35.94, -9.5) * mm});
            skLineSegment(sketch, "E94.5.3", {"start": v(-36.19, -9.36) * mm, "end": v(-36.44, -9.23) * mm});
            skLineSegment(sketch, "E94.5.4", {"start": v(-36.07, -9.15) * mm, "end": v(-35.72, -9.34) * mm});
            skLineSegment(sketch, "E94.5.5", {"start": v(-36.07, -9.15) * mm, "end": v(-36.41, -8.95) * mm});
            skLineSegment(sketch, "E94.5.6", {"start": v(-35.72, -9.34) * mm, "end": v(-35.26, -11.11) * mm});
            skLineSegment(sketch, "E94.5.7", {"start": v(-35.94, -9.5) * mm, "end": v(-35.65, -10.61) * mm});
            skLineSegment(sketch, "E94.5.8", {"start": v(-38.16, -9.51) * mm, "end": v(-35.26, -11.11) * mm});
            skLineSegment(sketch, "E94.5.9", {"start": v(-36.41, -8.95) * mm, "end": v(-38.16, -9.51) * mm});
            skLineSegment(sketch, "E94.6.0", {"start": v(-40.86, -9.23) * mm, "end": v(-41.27, -10.3) * mm});
            skLineSegment(sketch, "E94.6.1", {"start": v(-41.27, -10.3) * mm, "end": v(-39.28, -9.48) * mm});
            skLineSegment(sketch, "E94.6.2", {"start": v(-40.6, -9.12) * mm, "end": v(-40.33, -9) * mm});
            skLineSegment(sketch, "E94.6.3", {"start": v(-40.6, -9.12) * mm, "end": v(-40.86, -9.23) * mm});
            skLineSegment(sketch, "E94.6.4", {"start": v(-40.69, -8.89) * mm, "end": v(-40.32, -8.74) * mm});
            skLineSegment(sketch, "E94.6.5", {"start": v(-40.69, -8.89) * mm, "end": v(-41.05, -9.04) * mm});
            skLineSegment(sketch, "E94.6.6", {"start": v(-40.32, -8.74) * mm, "end": v(-38.65, -9.48) * mm});
            skLineSegment(sketch, "E94.6.7", {"start": v(-40.33, -9) * mm, "end": v(-39.28, -9.48) * mm});
            skLineSegment(sketch, "E94.6.8", {"start": v(-41.7, -10.75) * mm, "end": v(-38.65, -9.48) * mm});
            skLineSegment(sketch, "E94.6.9", {"start": v(-41.05, -9.04) * mm, "end": v(-41.7, -10.75) * mm});
            skCircle(sketch, "E95.cCircle", {"center": v(-38.64, -13.81) * mm, "radius": 2.75 * mm, "construction": true});
            skLineSegment(sketch, "E95.0", {"start": v(-37.9, -10.93) * mm, "end": v(-36.08, -12.3) * mm});
            skLineSegment(sketch, "E95.1", {"start": v(-36.08, -12.3) * mm, "end": v(-35.76, -14.55) * mm});
            skLineSegment(sketch, "E95.2", {"start": v(-35.76, -14.55) * mm, "end": v(-37.13, -16.38) * mm});
            skLineSegment(sketch, "E95.3", {"start": v(-37.13, -16.38) * mm, "end": v(-39.38, -16.7) * mm});
            skLineSegment(sketch, "E95.4", {"start": v(-39.38, -16.7) * mm, "end": v(-41.2, -15.33) * mm});
            skLineSegment(sketch, "E95.5", {"start": v(-41.2, -15.33) * mm, "end": v(-41.53, -13.07) * mm});
            skLineSegment(sketch, "E95.6", {"start": v(-41.53, -13.07) * mm, "end": v(-40.16, -11.25) * mm});
            skLineSegment(sketch, "E95.7", {"start": v(-40.16, -11.25) * mm, "end": v(-37.9, -10.93) * mm});
            skPoint(sketch, "E95.0.midPoint", {"position": v(-37, -11.61) * mm});
            skLineSegment(sketch, "E96", {"start": v(-40.16, -11.25) * mm, "end": v(-39.56, -10.45) * mm});
            skLineSegment(sketch, "E97", {"start": v(-37.9, -10.93) * mm, "end": v(-38.7, -10.33) * mm});
            skLineSegment(sketch, "E98", {"start": v(-39.56, -10.45) * mm, "end": v(-38.7, -10.33) * mm});
            skLineSegment(sketch, "E99.0", {"start": v(-39.5, -10.55) * mm, "end": v(-38.73, -10.44) * mm});
            skLineSegment(sketch, "E99.1", {"start": v(-39.94, -11.12) * mm, "end": v(-39.5, -10.55) * mm});
            skLineSegment(sketch, "E99.2", {"start": v(-39.94, -11.12) * mm, "end": v(-38.16, -10.87) * mm});
            skLineSegment(sketch, "E99.3", {"start": v(-38.16, -10.87) * mm, "end": v(-38.73, -10.44) * mm});
            skLineSegment(sketch, "E100.1.0", {"start": v(-41.3, -12.44) * mm, "end": v(-41.88, -12.85) * mm});
            skLineSegment(sketch, "E100.1.1", {"start": v(-41.16, -12.22) * mm, "end": v(-41.98, -12.8) * mm});
            skLineSegment(sketch, "E100.1.2", {"start": v(-42.02, -13.62) * mm, "end": v(-41.88, -12.85) * mm});
            skLineSegment(sketch, "E100.1.3", {"start": v(-42.12, -13.65) * mm, "end": v(-41.98, -12.8) * mm});
            skLineSegment(sketch, "E100.1.4", {"start": v(-41.55, -14.46) * mm, "end": v(-42.12, -13.65) * mm});
            skLineSegment(sketch, "E100.1.5", {"start": v(-41.6, -14.2) * mm, "end": v(-42.02, -13.62) * mm});
            skLineSegment(sketch, "E100.1.6", {"start": v(-41.6, -14.2) * mm, "end": v(-41.3, -12.44) * mm});
            skLineSegment(sketch, "E100.1.7", {"start": v(-41.55, -14.46) * mm, "end": v(-41.16, -12.22) * mm});
            skLineSegment(sketch, "E100.2.0", {"start": v(-40.77, -15.91) * mm, "end": v(-40.56, -16.6) * mm});
            skLineSegment(sketch, "E100.2.1", {"start": v(-40.94, -15.71) * mm, "end": v(-40.64, -16.67) * mm});
            skLineSegment(sketch, "E100.2.2", {"start": v(-39.87, -16.96) * mm, "end": v(-40.56, -16.6) * mm});
            skLineSegment(sketch, "E100.2.3", {"start": v(-39.88, -17.07) * mm, "end": v(-40.64, -16.67) * mm});
            skLineSegment(sketch, "E100.2.4", {"start": v(-38.92, -16.78) * mm, "end": v(-39.88, -17.07) * mm});
            skLineSegment(sketch, "E100.2.5", {"start": v(-39.18, -16.75) * mm, "end": v(-39.87, -16.96) * mm});
            skLineSegment(sketch, "E100.2.6", {"start": v(-39.18, -16.75) * mm, "end": v(-40.77, -15.91) * mm});
            skLineSegment(sketch, "E100.2.7", {"start": v(-38.92, -16.78) * mm, "end": v(-40.94, -15.71) * mm});
            skLineSegment(sketch, "E100.3.0", {"start": v(-37.3, -16.49) * mm, "end": v(-36.59, -16.5) * mm});
            skLineSegment(sketch, "E100.3.1", {"start": v(-37.55, -16.58) * mm, "end": v(-36.55, -16.6) * mm});
            skLineSegment(sketch, "E100.3.2", {"start": v(-36.03, -15.95) * mm, "end": v(-36.59, -16.5) * mm});
            skLineSegment(sketch, "E100.3.3", {"start": v(-35.93, -16) * mm, "end": v(-36.55, -16.6) * mm});
            skLineSegment(sketch, "E100.3.4", {"start": v(-35.91, -15) * mm, "end": v(-35.93, -16) * mm});
            skLineSegment(sketch, "E100.3.5", {"start": v(-36.02, -15.24) * mm, "end": v(-36.03, -15.95) * mm});
            skLineSegment(sketch, "E100.3.6", {"start": v(-36.02, -15.24) * mm, "end": v(-37.3, -16.49) * mm});
            skLineSegment(sketch, "E100.3.7", {"start": v(-35.91, -15) * mm, "end": v(-37.55, -16.58) * mm});
            skLineSegment(sketch, "E100.4.0", {"start": v(-35.7, -13.37) * mm, "end": v(-35.46, -12.69) * mm});
            skLineSegment(sketch, "E100.4.1", {"start": v(-35.67, -13.63) * mm, "end": v(-35.35, -12.68) * mm});
            skLineSegment(sketch, "E100.4.2", {"start": v(-35.8, -11.99) * mm, "end": v(-35.46, -12.69) * mm});
            skLineSegment(sketch, "E100.4.3", {"start": v(-35.73, -11.9) * mm, "end": v(-35.35, -12.68) * mm});
            skLineSegment(sketch, "E100.4.4", {"start": v(-36.68, -11.58) * mm, "end": v(-35.73, -11.9) * mm});
            skLineSegment(sketch, "E100.4.5", {"start": v(-36.48, -11.75) * mm, "end": v(-35.8, -11.99) * mm});
            skLineSegment(sketch, "E100.4.6", {"start": v(-36.48, -11.75) * mm, "end": v(-35.7, -13.37) * mm});
            skLineSegment(sketch, "E100.4.7", {"start": v(-36.68, -11.58) * mm, "end": v(-35.67, -13.63) * mm});
            skLineSegment(sketch, "E101", {"start": v(-41.4, -13.81) * mm, "end": v(-35.9, -13.81) * mm, "construction": true});
            skPoint(sketch, "E102", {"position": v(-37.31, -13.81) * mm});
            skPoint(sketch, "E103", {"position": v(-40.4, -13.81) * mm});
            skLineSegment(sketch, "E104", {"start": v(-39.85, -15.41) * mm, "end": v(-37.44, -12.21) * mm});
            skLineSegment(sketch, "E105", {"start": v(-37.44, -12.21) * mm, "end": v(-38.04, -11.76) * mm});
            skLineSegment(sketch, "E106.MirrorCS", {"start": v(-37.44, -12.21) * mm, "end": v(-36.84, -12.66) * mm});
            skLineSegment(sketch, "E107", {"start": v(-39.85, -15.41) * mm, "end": v(-39.25, -15.86) * mm});
            skLineSegment(sketch, "E108", {"start": v(-36.84, -12.66) * mm, "end": v(-39.25, -15.86) * mm});
            skLineSegment(sketch, "E109.MirrorCS", {"start": v(-39.85, -15.41) * mm, "end": v(-40.45, -14.96) * mm});
            skLineSegment(sketch, "E110", {"start": v(-40.45, -14.96) * mm, "end": v(-38.04, -11.76) * mm});
            skSolve(sketch);
        }
        {
            var Q0;
            {var subQ1=sQuery(id+"F6.wireOp",EDGE,"E70");var subQ2=sQuery(id+"F4.wireOp",EDGE,"E60.top");var subQ3=makeQuery(id+"F5.opExtrude","CAP_EDGE",EDGE,{"disambiguationData":[OSD([subQ2])],"isStart":false});var subQ4=makeQuery(id+"F6.imprint","INTERSECT",VERTEX,{"derivedFrom":[subQ3,subQ1]});var subQ7=makeQuery(id+"F6.imprint","IMPRINT",EDGE,{"disambiguationData":[TD([[subQ4,-1.0]])],"derivedFrom":subQ3});var subQ8=makeQuery(id+"F7.opExtrude","CAP_EDGE",EDGE,{"disambiguationData":[OSD([subQ2]),TDD([subQ7])],"isStart":false});Q0=makeQuery(id+"F12.imprint","IMPRINT",FACE,{"disambiguationData":[TD([[makeQuery(id+"F12.imprint","IMPRINT",EDGE,{"derivedFrom":subQ8}),1.0]])]});}
            var Q1;
            {var subQ5=sQuery(id+"F12.wireOp",EDGE,"E76");var subQ9=sQuery(id+"F12.wireOp",EDGE,"E83.4");var subQ11=makeQuery(id+"F12.imprint","INTERSECT",VERTEX,{"derivedFrom":[subQ5,subQ9]});Q1=makeQuery(id+"F12.imprint","IMPRINT",FACE,{"disambiguationData":[TD([[makeQuery(id+"F12.imprint","IMPRINT",EDGE,{"disambiguationData":[TD([[subQ11,-1.0]])],"derivedFrom":subQ5}),1.0]])]});}
            var Q2;
            {var subQ3=sQuery(id+"F12.wireOp",EDGE,"E76");var subQ5=makeQuery(id+"F5.opExtrude","CAP_EDGE",EDGE,{"disambiguationData":[OSD([sQuery(id+"F4.wireOp",EDGE,"E60.bottom")])],"isStart":false});var subQ6=makeQuery(id+"F12.imprint","INTERSECT",VERTEX,{"derivedFrom":[subQ5,subQ3]});Q2=makeQuery(id+"F12.imprint","IMPRINT",FACE,{"disambiguationData":[TD([[makeQuery(id+"F12.imprint","IMPRINT",EDGE,{"disambiguationData":[TD([[subQ6,1.0]])],"derivedFrom":subQ3}),1.0]])]});}
            var Q3;
            {var subQ1=sQuery(id+"F12.wireOp",EDGE,"E76");var subQ5=sQuery(id+"F12.wireOp",EDGE,"E94.2.8");var subQ9=makeQuery(id+"F12.imprint","INTERSECT",VERTEX,{"derivedFrom":[subQ1,subQ5]});Q3=makeQuery(id+"F12.imprint","IMPRINT",FACE,{"disambiguationData":[TD([[makeQuery(id+"F12.imprint","IMPRINT",EDGE,{"disambiguationData":[TD([[subQ9,-1.0]])],"derivedFrom":subQ1}),1.0]])]});}
            var Q4;
            {var subQ0=sQuery(id+"F12.wireOp",EDGE,"E94.2.1");var subQ1=sQuery(id+"F12.wireOp",EDGE,"E77");var subQ2=makeQuery(id+"F12.imprint","INTERSECT",VERTEX,{"derivedFrom":[subQ1,subQ0]});Q4=makeQuery(id+"F12.imprint","IMPRINT",FACE,{"disambiguationData":[TD([[makeQuery(id+"F12.imprint","IMPRINT",EDGE,{"disambiguationData":[TD([[subQ2,-1.0]])],"derivedFrom":subQ1}),-1.0]])]});}
            var Q5;
            {var subQ18=sQuery(id+"F12.wireOp",EDGE,"E94.2.2");Q5=makeQuery(id+"F12.imprint","IMPRINT",FACE,{"disambiguationData":[TD([[makeQuery(id+"F12.imprint","IMPRINT",EDGE,{"derivedFrom":subQ18}),1.0]])]});}
            var Q6;
            {var subQ0=sQuery(id+"F12.wireOp",EDGE,"E83.5");var subQ1=sQuery(id+"F12.wireOp",EDGE,"E83.4");var subQ2=makeQuery(id+"F12.imprint","INTERSECT",VERTEX,{"derivedFrom":[subQ1,subQ0]});Q6=makeQuery(id+"F12.imprint","IMPRINT",FACE,{"disambiguationData":[TD([[makeQuery(id+"F12.imprint","IMPRINT",EDGE,{"disambiguationData":[TD([[subQ2,1.0]])],"derivedFrom":subQ1}),-1.0]])]});}
            var Q7;
            {var subQ15=sQuery(id+"F12.wireOp",EDGE,"E94.2.2");Q7=makeQuery(id+"F12.imprint","IMPRINT",FACE,{"disambiguationData":[TD([[makeQuery(id+"F12.imprint","IMPRINT",EDGE,{"derivedFrom":subQ15}),-1.0]])]});}
            var Q8;
            {var subQ0=sQuery(id+"F12.wireOp",EDGE,"E94.2.1");var subQ1=sQuery(id+"F12.wireOp",EDGE,"E76");var subQ2=makeQuery(id+"F12.imprint","INTERSECT",VERTEX,{"derivedFrom":[subQ1,subQ0]});Q8=makeQuery(id+"F12.imprint","IMPRINT",FACE,{"disambiguationData":[TD([[makeQuery(id+"F12.imprint","IMPRINT",EDGE,{"disambiguationData":[TD([[subQ2,-1.0]])],"derivedFrom":subQ1}),1.0]])]});}
            var Q9;
            {var subQ0=sQuery(id+"F12.wireOp",EDGE,"E94.5.8");var subQ1=sQuery(id+"F12.wireOp",EDGE,"E76");var subQ2=makeQuery(id+"F12.imprint","INTERSECT",VERTEX,{"derivedFrom":[subQ1,subQ0]});Q9=makeQuery(id+"F12.imprint","IMPRINT",FACE,{"disambiguationData":[TD([[makeQuery(id+"F12.imprint","IMPRINT",EDGE,{"disambiguationData":[TD([[subQ2,-1.0]])],"derivedFrom":subQ1}),1.0]])]});}
            var Q10;
            {var subQ1=sQuery(id+"F12.wireOp",EDGE,"E83.0");var subQ3=sQuery(id+"F12.wireOp",EDGE,"E77");var subQ4=makeQuery(id+"F12.imprint","INTERSECT",VERTEX,{"derivedFrom":[subQ3,subQ1]});Q10=makeQuery(id+"F12.imprint","IMPRINT",FACE,{"disambiguationData":[TD([[makeQuery(id+"F12.imprint","IMPRINT",EDGE,{"disambiguationData":[TD([[subQ4,-1.0]])],"derivedFrom":subQ3}),-1.0]])]});}
            var Q11;
            {var subQ0=sQuery(id+"F12.wireOp",EDGE,"E94.6.1");var subQ1=sQuery(id+"F12.wireOp",EDGE,"E77");var subQ2=makeQuery(id+"F12.imprint","INTERSECT",VERTEX,{"derivedFrom":[subQ1,subQ0]});Q11=makeQuery(id+"F12.imprint","IMPRINT",FACE,{"disambiguationData":[TD([[makeQuery(id+"F12.imprint","IMPRINT",EDGE,{"disambiguationData":[TD([[subQ2,-1.0]])],"derivedFrom":subQ1}),-1.0]])]});}
            var Q12;
            {var subQ0=sQuery(id+"F12.wireOp",EDGE,"E94.6.8");var subQ1=sQuery(id+"F12.wireOp",EDGE,"E77");var subQ2=makeQuery(id+"F12.imprint","INTERSECT",VERTEX,{"derivedFrom":[subQ1,subQ0]});Q12=makeQuery(id+"F12.imprint","IMPRINT",FACE,{"disambiguationData":[TD([[makeQuery(id+"F12.imprint","IMPRINT",EDGE,{"disambiguationData":[TD([[subQ2,-1.0]])],"derivedFrom":subQ1}),-1.0]])]});}
            var Q13;
            {var subQ5=sQuery(id+"F12.wireOp",EDGE,"E76");var subQ8=sQuery(id+"F12.wireOp",EDGE,"E97");var subQ10=makeQuery(id+"F12.imprint","INTERSECT",VERTEX,{"derivedFrom":[subQ5,subQ8]});Q13=makeQuery(id+"F12.imprint","IMPRINT",FACE,{"disambiguationData":[TD([[makeQuery(id+"F12.imprint","IMPRINT",EDGE,{"disambiguationData":[TD([[subQ10,-1.0]])],"derivedFrom":subQ5}),1.0]])]});}
            var Q14;
            {var subQ7=sQuery(id+"F12.wireOp",EDGE,"E99.3");Q14=makeQuery(id+"F12.imprint","IMPRINT",FACE,{"disambiguationData":[TD([[makeQuery(id+"F12.imprint","IMPRINT",EDGE,{"derivedFrom":subQ7}),-1.0]])]});}
            var Q15;
            {var subQ5=sQuery(id+"F12.wireOp",EDGE,"E99.3");Q15=makeQuery(id+"F12.imprint","IMPRINT",FACE,{"disambiguationData":[TD([[makeQuery(id+"F12.imprint","IMPRINT",EDGE,{"derivedFrom":subQ5}),1.0]])]});}
            var Q16;
            {var subQ0=sQuery(id+"F12.wireOp",EDGE,"E95.3");var subQ1=sQuery(id+"F12.wireOp",EDGE,"E76");var subQ2=makeQuery(id+"F12.imprint","INTERSECT",VERTEX,{"derivedFrom":[subQ1,subQ0]});Q16=makeQuery(id+"F12.imprint","IMPRINT",FACE,{"disambiguationData":[TD([[makeQuery(id+"F12.imprint","IMPRINT",EDGE,{"disambiguationData":[TD([[subQ2,-1.0]])],"derivedFrom":subQ1}),1.0]])]});}
            var Q17;
            {var subQ3=sQuery(id+"F12.wireOp",EDGE,"E77");var subQ9=sQuery(id+"F12.wireOp",EDGE,"E100.2.4");var subQ11=makeQuery(id+"F12.imprint","INTERSECT",VERTEX,{"derivedFrom":[subQ3,subQ9]});Q17=makeQuery(id+"F12.imprint","IMPRINT",FACE,{"disambiguationData":[TD([[makeQuery(id+"F12.imprint","IMPRINT",EDGE,{"disambiguationData":[TD([[subQ11,-1.0]])],"derivedFrom":subQ3}),-1.0]])]});}
            var Q18;
            {var subQ0=sQuery(id+"F12.wireOp",EDGE,"E100.2.5");var subQ1=sQuery(id+"F12.wireOp",EDGE,"E77");var subQ2=makeQuery(id+"F12.imprint","INTERSECT",VERTEX,{"derivedFrom":[subQ1,subQ0]});Q18=makeQuery(id+"F12.imprint","IMPRINT",FACE,{"disambiguationData":[TD([[makeQuery(id+"F12.imprint","IMPRINT",EDGE,{"disambiguationData":[TD([[subQ2,-1.0]])],"derivedFrom":subQ1}),-1.0]])]});}
            var Q19;
            {var subQ0=sQuery(id+"F12.wireOp",EDGE,"E100.2.6");var subQ1=sQuery(id+"F12.wireOp",EDGE,"E77");var subQ2=makeQuery(id+"F12.imprint","INTERSECT",VERTEX,{"derivedFrom":[subQ1,subQ0]});Q19=makeQuery(id+"F12.imprint","IMPRINT",FACE,{"disambiguationData":[TD([[makeQuery(id+"F12.imprint","IMPRINT",EDGE,{"disambiguationData":[TD([[subQ2,-1.0]])],"derivedFrom":subQ1}),-1.0]])]});}
            var Q20;
            {var subQ0=sQuery(id+"F12.wireOp",EDGE,"E83.cCircle");var subQ1=sQuery(id+"F12.wireOp",EDGE,"E76");var subQ2=makeQuery(id+"F12.imprint","INTERSECT",VERTEX,{"disambiguationData":[OD(0.0)],"derivedFrom":[subQ1,subQ0]});Q20=makeQuery(id+"F12.imprint","IMPRINT",FACE,{"disambiguationData":[TD([[makeQuery(id+"F12.imprint","IMPRINT",EDGE,{"disambiguationData":[TD([[subQ2,-1.0]])],"derivedFrom":subQ1}),1.0]])]});}
            var Q21;
            {var subQ1=sQuery(id+"F12.wireOp",EDGE,"E105");var subQ3=sQuery(id+"F12.wireOp",EDGE,"E76");var subQ4=makeQuery(id+"F12.imprint","INTERSECT",VERTEX,{"derivedFrom":[subQ3,subQ1]});Q21=makeQuery(id+"F12.imprint","IMPRINT",FACE,{"disambiguationData":[TD([[makeQuery(id+"F12.imprint","IMPRINT",EDGE,{"disambiguationData":[TD([[subQ4,-1.0]])],"derivedFrom":subQ3}),1.0]])]});}
            var Q22;
            {var subQ0=sQuery(id+"F12.wireOp",EDGE,"E104");var subQ1=sQuery(id+"F12.wireOp",EDGE,"E76");var subQ2=makeQuery(id+"F12.imprint","INTERSECT",VERTEX,{"derivedFrom":[subQ1,subQ0]});Q22=makeQuery(id+"F12.imprint","IMPRINT",FACE,{"disambiguationData":[TD([[makeQuery(id+"F12.imprint","IMPRINT",EDGE,{"disambiguationData":[TD([[subQ2,-1.0]])],"derivedFrom":subQ1}),1.0]])]});}
            var Q23;
            {var subQ0=sQuery(id+"F12.wireOp",EDGE,"E108");var subQ6=sQuery(id+"F12.wireOp",EDGE,"E76");var subQ9=makeQuery(id+"F12.imprint","INTERSECT",VERTEX,{"derivedFrom":[subQ6,subQ0]});Q23=makeQuery(id+"F12.imprint","IMPRINT",FACE,{"disambiguationData":[TD([[makeQuery(id+"F12.imprint","IMPRINT",EDGE,{"disambiguationData":[TD([[subQ9,-1.0]])],"derivedFrom":subQ6}),1.0]])]});}
            var Q24;
            {var subQ1=sQuery(id+"F12.wireOp",EDGE,"E76");var subQ5=sQuery(id+"F12.wireOp",EDGE,"E83.cCircle");var subQ6=makeQuery(id+"F12.imprint","INTERSECT",VERTEX,{"disambiguationData":[OD(1.0)],"derivedFrom":[subQ1,subQ5]});Q24=makeQuery(id+"F12.imprint","IMPRINT",FACE,{"disambiguationData":[TD([[makeQuery(id+"F12.imprint","IMPRINT",EDGE,{"disambiguationData":[TD([[subQ6,-1.0]])],"derivedFrom":subQ1}),1.0]])]});}
            extrude(context, id + "F13", {"entities" : qUnion([Q0, Q1, Q2, Q3, Q4, Q5, Q6, Q7, Q8, Q9, Q10, Q11, Q12, Q13, Q14, Q15, Q16, Q17, Q18, Q19, Q20, Q21, Q22, Q23, Q24]), "operationType" : NewBodyOperationType.ADD, "depth" : 1 * mm});
        }
        {
            var Q0;
            {var subQ0=sQuery(id+"F4.wireOp",EDGE,"E60.bottom");Q0=makeQuery(id+"F13.boolean.opBoolean","MERGE",FACE,{"derivedFrom":[makeQuery(id+"F11.boolean.opBoolean","MERGE",FACE,{"derivedFrom":[makeQuery(id+"F9.boolean.opBoolean","MERGE",FACE,{"derivedFrom":[makeQuery(id+"F5.opExtrude","SWEPT_FACE",FACE,{"disambiguationData":[OSD([subQ0])]}),makeQuery(id+"F9.opExtrude","SWEPT_FACE",FACE,{"disambiguationData":[OSD([subQ0,sQuery(id+"F4.wireOp",EDGE,"E60.left")])]})]}),makeQuery(id+"F11.opExtrude","SWEPT_FACE",FACE,{"disambiguationData":[OSD([subQ0,sQuery(id+"F4.wireOp",EDGE,"E60.right")])]})]}),makeQuery(id+"F13.opExtrude","SWEPT_FACE",FACE,{"disambiguationData":[OSD([subQ0])]})]});}
            var sketch = newSketch(context, id + "F14", { "sketchPlane" : qUnion([Q0])});
            skLineSegment(sketch, "E111", {"start": v(32.64, 4.33) * mm, "end": v(44.64, 4.33) * mm});
            skLineSegment(sketch, "E112", {"start": v(32.64, 5.67) * mm, "end": v(44.64, 5.67) * mm});
            skLineSegment(sketch, "E113", {"start": v(37.98, 11) * mm, "end": v(37.98, 0) * mm});
            skLineSegment(sketch, "E114", {"start": v(39.31, 11) * mm, "end": v(39.31, 0) * mm});
            skSolve(sketch);
        }
        {
            var Q0;
            {var subQ0=sQuery(id+"F14.wireOp",EDGE,"E113");var subQ1=sQuery(id+"F14.wireOp",EDGE,"E111");var subQ2=makeQuery(id+"F14.imprint","INTERSECT",VERTEX,{"derivedFrom":[subQ1,subQ0]});Q0=makeQuery(id+"F14.imprint","IMPRINT",FACE,{"disambiguationData":[TD([[makeQuery(id+"F14.imprint","IMPRINT",EDGE,{"disambiguationData":[TD([[subQ2,-1.0]])],"derivedFrom":subQ1}),1.0]])]});}
            var Q1;
            {var subQ1=sQuery(id+"F4.wireOp",EDGE,"E60.left");var subQ2=sQuery(id+"F4.wireOp",EDGE,"E60.bottom");var subQ3=makeQuery(id+"F9.opExtrude","CAP_EDGE",EDGE,{"disambiguationData":[OSD([subQ2,subQ1])],"isStart":false});Q1=makeQuery(id+"F14.imprint","IMPRINT",FACE,{"disambiguationData":[TD([[makeQuery(id+"F14.imprint","IMPRINT",EDGE,{"derivedFrom":subQ3}),-1.0]])]});}
            var Q2;
            {var subQ8=sQuery(id+"F4.wireOp",EDGE,"E60.bottom");var subQ22=makeQuery(id+"F13.opExtrude","CAP_EDGE",EDGE,{"disambiguationData":[OSD([subQ8])],"isStart":false});Q2=makeQuery(id+"F14.imprint","IMPRINT",FACE,{"disambiguationData":[TD([[makeQuery(id+"F14.imprint","IMPRINT",EDGE,{"derivedFrom":subQ22}),1.0]])]});}
            var Q3;
            {var subQ1=sQuery(id+"F4.wireOp",EDGE,"E60.right");var subQ2=sQuery(id+"F4.wireOp",EDGE,"E60.bottom");var subQ3=makeQuery(id+"F11.opExtrude","CAP_EDGE",EDGE,{"disambiguationData":[OSD([subQ2,subQ1])],"isStart":false});Q3=makeQuery(id+"F14.imprint","IMPRINT",FACE,{"disambiguationData":[TD([[makeQuery(id+"F14.imprint","IMPRINT",EDGE,{"derivedFrom":subQ3}),1.0]])]});}
            var Q4;
            {var subQ0=sQuery(id+"F14.wireOp",EDGE,"E113");var subQ1=sQuery(id+"F14.wireOp",EDGE,"E111");var subQ2=makeQuery(id+"F14.imprint","INTERSECT",VERTEX,{"derivedFrom":[subQ1,subQ0]});Q4=makeQuery(id+"F14.imprint","IMPRINT",FACE,{"disambiguationData":[TD([[makeQuery(id+"F14.imprint","IMPRINT",EDGE,{"disambiguationData":[TD([[subQ2,-1.0]])],"derivedFrom":subQ1}),-1.0]])]});}
            extrude(context, id + "F15", {"entities" : qUnion([Q0, Q1, Q2, Q3, Q4]), "operationType" : NewBodyOperationType.ADD, "depth" : 1 * mm});
        }
        {
            var Q0;
            {var subQ5=sQuery(id+"F12.wireOp",EDGE,"E89");Q0=makeQuery(id+"F12.imprint","IMPRINT",FACE,{"disambiguationData":[TD([[makeQuery(id+"F12.imprint","IMPRINT",EDGE,{"derivedFrom":subQ5}),-1.0]])]});}
            var Q1;
            {var subQ0=sQuery(id+"F12.wireOp",EDGE,"E83.7");Q1=makeQuery(id+"F12.imprint","IMPRINT",FACE,{"disambiguationData":[TD([[makeQuery(id+"F12.imprint","IMPRINT",EDGE,{"derivedFrom":subQ0}),1.0]])]});}
            var Q2;
            Q2=makeQuery(id+"F12.imprint","IMPRINT",FACE,{"disambiguationData":[TD([[makeQuery(id+"F12.imprint","IMPRINT",EDGE,{"derivedFrom":sQuery(id+"F12.wireOp",EDGE,"E94.1.0")}),-1.0]])]});
            var Q3;
            {var subQ1=sQuery(id+"F12.wireOp",EDGE,"E94.2.1");var subQ3=sQuery(id+"F12.wireOp",EDGE,"E77");var subQ4=makeQuery(id+"F12.imprint","INTERSECT",VERTEX,{"derivedFrom":[subQ3,subQ1]});Q3=makeQuery(id+"F12.imprint","IMPRINT",FACE,{"disambiguationData":[TD([[makeQuery(id+"F12.imprint","IMPRINT",EDGE,{"disambiguationData":[TD([[subQ4,-1.0]])],"derivedFrom":subQ3}),1.0]])]});}
            var Q4;
            {var subQ8=sQuery(id+"F12.wireOp",EDGE,"E94.2.4");var subQ10=sQuery(id+"F12.wireOp",EDGE,"E94.2.6");var subQ11=makeQuery(id+"F12.imprint","INTERSECT",VERTEX,{"derivedFrom":[subQ8,subQ10]});Q4=makeQuery(id+"F12.imprint","IMPRINT",FACE,{"disambiguationData":[TD([[makeQuery(id+"F12.imprint","IMPRINT",EDGE,{"disambiguationData":[TD([[subQ11,1.0]])],"derivedFrom":subQ8}),-1.0]])]});}
            var Q5;
            {var subQ3=sQuery(id+"F12.wireOp",EDGE,"E76");var subQ5=sQuery(id+"F12.wireOp",EDGE,"E94.2.9");var subQ6=makeQuery(id+"F12.imprint","INTERSECT",VERTEX,{"derivedFrom":[subQ3,subQ5]});Q5=makeQuery(id+"F12.imprint","IMPRINT",FACE,{"disambiguationData":[TD([[makeQuery(id+"F12.imprint","IMPRINT",EDGE,{"disambiguationData":[TD([[subQ6,-1.0]])],"derivedFrom":subQ3}),-1.0]])]});}
            var Q6;
            {var subQ11=sQuery(id+"F12.wireOp",EDGE,"E94.3.0");Q6=makeQuery(id+"F12.imprint","IMPRINT",FACE,{"disambiguationData":[TD([[makeQuery(id+"F12.imprint","IMPRINT",EDGE,{"derivedFrom":subQ11}),-1.0]])]});}
            var Q7;
            {var subQ0=sQuery(id+"F12.wireOp",EDGE,"E94.3.8");var subQ1=sQuery(id+"F12.wireOp",EDGE,"E83.3");var subQ2=makeQuery(id+"F12.imprint","INTERSECT",VERTEX,{"derivedFrom":[subQ1,subQ0]});Q7=makeQuery(id+"F12.imprint","IMPRINT",FACE,{"disambiguationData":[TD([[makeQuery(id+"F12.imprint","IMPRINT",EDGE,{"disambiguationData":[TD([[subQ2,-1.0]])],"derivedFrom":subQ1}),-1.0]])]});}
            var Q8;
            {var subQ1=sQuery(id+"F12.wireOp",EDGE,"E94.4.0");Q8=makeQuery(id+"F12.imprint","IMPRINT",FACE,{"disambiguationData":[TD([[makeQuery(id+"F12.imprint","IMPRINT",EDGE,{"derivedFrom":subQ1}),-1.0]])]});}
            var Q9;
            {var subQ0=sQuery(id+"F12.wireOp",EDGE,"E94.4.8");var subQ1=sQuery(id+"F12.wireOp",EDGE,"E83.2");var subQ2=makeQuery(id+"F12.imprint","INTERSECT",VERTEX,{"derivedFrom":[subQ1,subQ0]});Q9=makeQuery(id+"F12.imprint","IMPRINT",FACE,{"disambiguationData":[TD([[makeQuery(id+"F12.imprint","IMPRINT",EDGE,{"disambiguationData":[TD([[subQ2,-1.0]])],"derivedFrom":subQ1}),-1.0]])]});}
            var Q10;
            {var subQ3=sQuery(id+"F12.wireOp",EDGE,"E94.4.2");Q10=makeQuery(id+"F12.imprint","IMPRINT",FACE,{"disambiguationData":[TD([[makeQuery(id+"F12.imprint","IMPRINT",EDGE,{"derivedFrom":subQ3}),1.0]])]});}
            var Q11;
            {var subQ5=sQuery(id+"F12.wireOp",EDGE,"E94.4.1");var subQ6=sQuery(id+"F12.wireOp",EDGE,"E83.3");var subQ7=makeQuery(id+"F12.imprint","INTERSECT",VERTEX,{"derivedFrom":[subQ6,subQ5]});Q11=makeQuery(id+"F12.imprint","IMPRINT",FACE,{"disambiguationData":[TD([[makeQuery(id+"F12.imprint","IMPRINT",EDGE,{"disambiguationData":[TD([[subQ7,-1.0]])],"derivedFrom":subQ6}),1.0]])]});}
            var Q12;
            {var subQ0=sQuery(id+"F12.wireOp",EDGE,"E94.5.8");var subQ1=sQuery(id+"F12.wireOp",EDGE,"E83.1");var subQ2=makeQuery(id+"F12.imprint","INTERSECT",VERTEX,{"derivedFrom":[subQ1,subQ0]});Q12=makeQuery(id+"F12.imprint","IMPRINT",FACE,{"disambiguationData":[TD([[makeQuery(id+"F12.imprint","IMPRINT",EDGE,{"disambiguationData":[TD([[subQ2,-1.0]])],"derivedFrom":subQ1}),-1.0]])]});}
            var Q13;
            {var subQ5=sQuery(id+"F12.wireOp",EDGE,"E94.5.0");Q13=makeQuery(id+"F12.imprint","IMPRINT",FACE,{"disambiguationData":[TD([[makeQuery(id+"F12.imprint","IMPRINT",EDGE,{"derivedFrom":subQ5}),-1.0]])]});}
            var Q14;
            {var subQ10=sQuery(id+"F12.wireOp",EDGE,"E94.6.0");Q14=makeQuery(id+"F12.imprint","IMPRINT",FACE,{"disambiguationData":[TD([[makeQuery(id+"F12.imprint","IMPRINT",EDGE,{"derivedFrom":subQ10}),-1.0]])]});}
            var Q15;
            {var subQ0=sQuery(id+"F12.wireOp",EDGE,"E94.6.6");var subQ1=sQuery(id+"F12.wireOp",EDGE,"E94.6.4");var subQ2=makeQuery(id+"F12.imprint","INTERSECT",VERTEX,{"derivedFrom":[subQ1,subQ0]});Q15=makeQuery(id+"F12.imprint","IMPRINT",FACE,{"disambiguationData":[TD([[makeQuery(id+"F12.imprint","IMPRINT",EDGE,{"disambiguationData":[TD([[subQ2,1.0]])],"derivedFrom":subQ1}),-1.0]])]});}
            var Q16;
            {var subQ0=sQuery(id+"F12.wireOp",EDGE,"E83.4");var subQ1=sQuery(id+"F12.wireOp",EDGE,"E76");var subQ2=makeQuery(id+"F12.imprint","INTERSECT",VERTEX,{"derivedFrom":[subQ1,subQ0]});Q16=makeQuery(id+"F12.imprint","IMPRINT",FACE,{"disambiguationData":[TD([[makeQuery(id+"F12.imprint","IMPRINT",EDGE,{"disambiguationData":[TD([[subQ2,-1.0]])],"derivedFrom":subQ1}),-1.0]])]});}
            var Q17;
            {var subQ18=sQuery(id+"F12.wireOp",EDGE,"E94.2.2");Q17=makeQuery(id+"F12.imprint","IMPRINT",FACE,{"disambiguationData":[TD([[makeQuery(id+"F12.imprint","IMPRINT",EDGE,{"derivedFrom":subQ18}),1.0]])]});}
            var Q18;
            {var subQ1=sQuery(id+"F12.wireOp",EDGE,"E83.0");var subQ3=sQuery(id+"F12.wireOp",EDGE,"E77");var subQ4=makeQuery(id+"F12.imprint","INTERSECT",VERTEX,{"derivedFrom":[subQ3,subQ1]});Q18=makeQuery(id+"F12.imprint","IMPRINT",FACE,{"disambiguationData":[TD([[makeQuery(id+"F12.imprint","IMPRINT",EDGE,{"disambiguationData":[TD([[subQ4,-1.0]])],"derivedFrom":subQ3}),-1.0]])]});}
            var Q19;
            {var subQ0=sQuery(id+"F12.wireOp",EDGE,"E94.6.8");var subQ1=sQuery(id+"F12.wireOp",EDGE,"E77");var subQ2=makeQuery(id+"F12.imprint","INTERSECT",VERTEX,{"derivedFrom":[subQ1,subQ0]});Q19=makeQuery(id+"F12.imprint","IMPRINT",FACE,{"disambiguationData":[TD([[makeQuery(id+"F12.imprint","IMPRINT",EDGE,{"disambiguationData":[TD([[subQ2,-1.0]])],"derivedFrom":subQ1}),-1.0]])]});}
            var Q20;
            {var subQ0=sQuery(id+"F12.wireOp",EDGE,"E94.6.8");var subQ1=sQuery(id+"F12.wireOp",EDGE,"E77");var subQ2=makeQuery(id+"F12.imprint","INTERSECT",VERTEX,{"derivedFrom":[subQ1,subQ0]});Q20=makeQuery(id+"F12.imprint","IMPRINT",FACE,{"disambiguationData":[TD([[makeQuery(id+"F12.imprint","IMPRINT",EDGE,{"disambiguationData":[TD([[subQ2,-1.0]])],"derivedFrom":subQ1}),1.0]])]});}
            var Q21;
            {var subQ0=sQuery(id+"F12.wireOp",EDGE,"E94.2.1");var subQ1=sQuery(id+"F12.wireOp",EDGE,"E77");var subQ2=makeQuery(id+"F12.imprint","INTERSECT",VERTEX,{"derivedFrom":[subQ1,subQ0]});Q21=makeQuery(id+"F12.imprint","IMPRINT",FACE,{"disambiguationData":[TD([[makeQuery(id+"F12.imprint","IMPRINT",EDGE,{"disambiguationData":[TD([[subQ2,-1.0]])],"derivedFrom":subQ1}),-1.0]])]});}
            var Q22;
            {var subQ7=sQuery(id+"F12.wireOp",EDGE,"E83.4");var subQ8=sQuery(id+"F12.wireOp",EDGE,"E76");var subQ9=makeQuery(id+"F12.imprint","INTERSECT",VERTEX,{"derivedFrom":[subQ8,subQ7]});Q22=makeQuery(id+"F12.imprint","IMPRINT",FACE,{"disambiguationData":[TD([[makeQuery(id+"F12.imprint","IMPRINT",EDGE,{"disambiguationData":[TD([[subQ9,-1.0]])],"derivedFrom":subQ8}),1.0]])]});}
            var Q23;
            {var subQ0=sQuery(id+"F12.wireOp",EDGE,"E94.2.1");var subQ1=sQuery(id+"F12.wireOp",EDGE,"E76");var subQ2=makeQuery(id+"F12.imprint","INTERSECT",VERTEX,{"derivedFrom":[subQ1,subQ0]});Q23=makeQuery(id+"F12.imprint","IMPRINT",FACE,{"disambiguationData":[TD([[makeQuery(id+"F12.imprint","IMPRINT",EDGE,{"disambiguationData":[TD([[subQ2,-1.0]])],"derivedFrom":subQ1}),1.0]])]});}
            extrude(context, id + "F16", {"entities" : qUnion([Q0, Q1, Q2, Q3, Q4, Q5, Q6, Q7, Q8, Q9, Q10, Q11, Q12, Q13, Q14, Q15, Q16, Q17, Q18, Q19, Q20, Q21, Q22, Q23]), "operationType" : NewBodyOperationType.ADD, "depth" : 3 / 4 * mm});
        }
        {
            var Q0;
            {var subQ0=sQuery(id+"F12.wireOp",EDGE,"E96");Q0=makeQuery(id+"F12.imprint","IMPRINT",FACE,{"disambiguationData":[TD([[makeQuery(id+"F12.imprint","IMPRINT",EDGE,{"derivedFrom":subQ0}),-1.0]])]});}
            var Q1;
            {var subQ7=sQuery(id+"F12.wireOp",EDGE,"E99.3");Q1=makeQuery(id+"F12.imprint","IMPRINT",FACE,{"disambiguationData":[TD([[makeQuery(id+"F12.imprint","IMPRINT",EDGE,{"derivedFrom":subQ7}),-1.0]])]});}
            var Q2;
            {var subQ0=sQuery(id+"F12.wireOp",EDGE,"E95.7");var subQ1=sQuery(id+"F12.wireOp",EDGE,"E76");var subQ2=makeQuery(id+"F12.imprint","INTERSECT",VERTEX,{"derivedFrom":[subQ1,subQ0]});Q2=makeQuery(id+"F12.imprint","IMPRINT",FACE,{"disambiguationData":[TD([[makeQuery(id+"F12.imprint","IMPRINT",EDGE,{"disambiguationData":[TD([[subQ2,-1.0]])],"derivedFrom":subQ1}),-1.0]])]});}
            var Q3;
            {var subQ1=sQuery(id+"F12.wireOp",EDGE,"E100.1.0");Q3=makeQuery(id+"F12.imprint","IMPRINT",FACE,{"disambiguationData":[TD([[makeQuery(id+"F12.imprint","IMPRINT",EDGE,{"derivedFrom":subQ1}),-1.0]])]});}
            var Q4;
            {var subQ0=sQuery(id+"F12.wireOp",EDGE,"E100.1.7");var subQ1=sQuery(id+"F12.wireOp",EDGE,"E95.5");var subQ2=makeQuery(id+"F12.imprint","INTERSECT",VERTEX,{"derivedFrom":[subQ1,subQ0]});Q4=makeQuery(id+"F12.imprint","IMPRINT",FACE,{"disambiguationData":[TD([[makeQuery(id+"F12.imprint","IMPRINT",EDGE,{"disambiguationData":[TD([[subQ2,-1.0]])],"derivedFrom":subQ1}),-1.0]])]});}
            var Q5;
            {var subQ0=sQuery(id+"F12.wireOp",EDGE,"E100.2.0");Q5=makeQuery(id+"F12.imprint","IMPRINT",FACE,{"disambiguationData":[TD([[makeQuery(id+"F12.imprint","IMPRINT",EDGE,{"derivedFrom":subQ0}),-1.0]])]});}
            var Q6;
            {var subQ0=sQuery(id+"F12.wireOp",EDGE,"E100.2.6");var subQ1=sQuery(id+"F12.wireOp",EDGE,"E77");var subQ2=makeQuery(id+"F12.imprint","INTERSECT",VERTEX,{"derivedFrom":[subQ1,subQ0]});Q6=makeQuery(id+"F12.imprint","IMPRINT",FACE,{"disambiguationData":[TD([[makeQuery(id+"F12.imprint","IMPRINT",EDGE,{"disambiguationData":[TD([[subQ2,-1.0]])],"derivedFrom":subQ1}),1.0]])]});}
            var Q7;
            {var subQ0=sQuery(id+"F12.wireOp",EDGE,"E100.2.6");var subQ1=sQuery(id+"F12.wireOp",EDGE,"E77");var subQ2=makeQuery(id+"F12.imprint","INTERSECT",VERTEX,{"derivedFrom":[subQ1,subQ0]});Q7=makeQuery(id+"F12.imprint","IMPRINT",FACE,{"disambiguationData":[TD([[makeQuery(id+"F12.imprint","IMPRINT",EDGE,{"disambiguationData":[TD([[subQ2,-1.0]])],"derivedFrom":subQ1}),-1.0]])]});}
            var Q8;
            {var subQ3=sQuery(id+"F12.wireOp",EDGE,"E77");var subQ9=sQuery(id+"F12.wireOp",EDGE,"E100.2.4");var subQ11=makeQuery(id+"F12.imprint","INTERSECT",VERTEX,{"derivedFrom":[subQ3,subQ9]});Q8=makeQuery(id+"F12.imprint","IMPRINT",FACE,{"disambiguationData":[TD([[makeQuery(id+"F12.imprint","IMPRINT",EDGE,{"disambiguationData":[TD([[subQ11,-1.0]])],"derivedFrom":subQ3}),-1.0]])]});}
            var Q9;
            {var subQ1=sQuery(id+"F12.wireOp",EDGE,"E100.3.0");Q9=makeQuery(id+"F12.imprint","IMPRINT",FACE,{"disambiguationData":[TD([[makeQuery(id+"F12.imprint","IMPRINT",EDGE,{"derivedFrom":subQ1}),-1.0]])]});}
            var Q10;
            {var subQ0=sQuery(id+"F12.wireOp",EDGE,"E100.3.7");var subQ1=sQuery(id+"F12.wireOp",EDGE,"E95.2");var subQ2=makeQuery(id+"F12.imprint","INTERSECT",VERTEX,{"derivedFrom":[subQ1,subQ0]});Q10=makeQuery(id+"F12.imprint","IMPRINT",FACE,{"disambiguationData":[TD([[makeQuery(id+"F12.imprint","IMPRINT",EDGE,{"disambiguationData":[TD([[subQ2,-1.0]])],"derivedFrom":subQ1}),-1.0]])]});}
            var Q11;
            {var subQ1=sQuery(id+"F12.wireOp",EDGE,"E100.4.0");Q11=makeQuery(id+"F12.imprint","IMPRINT",FACE,{"disambiguationData":[TD([[makeQuery(id+"F12.imprint","IMPRINT",EDGE,{"derivedFrom":subQ1}),-1.0]])]});}
            var Q12;
            {var subQ0=sQuery(id+"F12.wireOp",EDGE,"E100.4.7");var subQ1=sQuery(id+"F12.wireOp",EDGE,"E95.0");var subQ2=makeQuery(id+"F12.imprint","INTERSECT",VERTEX,{"derivedFrom":[subQ1,subQ0]});Q12=makeQuery(id+"F12.imprint","IMPRINT",FACE,{"disambiguationData":[TD([[makeQuery(id+"F12.imprint","IMPRINT",EDGE,{"disambiguationData":[TD([[subQ2,-1.0]])],"derivedFrom":subQ1}),-1.0]])]});}
            extrude(context, id + "F17", {"entities" : qUnion([Q0, Q1, Q2, Q3, Q4, Q5, Q6, Q7, Q8, Q9, Q10, Q11, Q12]), "operationType" : NewBodyOperationType.ADD, "depth" : 3 / 2 * mm});
        }
        {
            var Q0;
            Q0=makeQuery(id+"F17.opExtrude","CAP_FACE",FACE,{"disambiguationData":[OSD([sQuery(id+"F12.wireOp",EDGE,"E95.7"),sQuery(id+"F12.wireOp",EDGE,"E96"),sQuery(id+"F12.wireOp",EDGE,"E97"),sQuery(id+"F12.wireOp",EDGE,"E98"),sQuery(id+"F12.wireOp",EDGE,"E99.0"),sQuery(id+"F12.wireOp",EDGE,"E99.1"),sQuery(id+"F12.wireOp",EDGE,"E99.2"),sQuery(id+"F12.wireOp",EDGE,"E99.3")])],"isStart":false});
            var Q1;
            Q1=makeQuery(id+"F17.opExtrude","CAP_EDGE",EDGE,{"disambiguationData":[OSD([sQuery(id+"F12.wireOp",EDGE,"E95.7")])],"isStart":false});
            revolve(context, id + "F18", {"operationType" : NewBodyOperationType.ADD, "entities" : qUnion([Q0]), "axis" : qUnion([Q1]), "revolveType" : RevolveType.ONE_DIRECTION, "angle" : PI / 4 * radian});
        }
        {
            var Q0;
            Q0=makeQuery(id+"F17.opExtrude","CAP_FACE",FACE,{"disambiguationData":[OSD([sQuery(id+"F12.wireOp",EDGE,"E100.1.0"),sQuery(id+"F12.wireOp",EDGE,"E100.1.1"),sQuery(id+"F12.wireOp",EDGE,"E100.1.2"),sQuery(id+"F12.wireOp",EDGE,"E100.1.3"),sQuery(id+"F12.wireOp",EDGE,"E100.1.4"),sQuery(id+"F12.wireOp",EDGE,"E100.1.5"),sQuery(id+"F12.wireOp",EDGE,"E100.1.6"),sQuery(id+"F12.wireOp",EDGE,"E100.1.7")])],"isStart":false});
            var Q1;
            Q1=makeQuery(id+"F17.opExtrude","CAP_EDGE",EDGE,{"disambiguationData":[OSD([sQuery(id+"F12.wireOp",EDGE,"E100.1.7")])],"isStart":false});
            revolve(context, id + "F19", {"operationType" : NewBodyOperationType.ADD, "entities" : qUnion([Q0]), "axis" : qUnion([Q1]), "revolveType" : RevolveType.ONE_DIRECTION, "angle" : (PI / 4) * radian});
        }
        {
            var Q0;
            Q0=makeQuery(id+"F17.opExtrude","CAP_FACE",FACE,{"disambiguationData":[OSD([sQuery(id+"F12.wireOp",EDGE,"E100.4.0"),sQuery(id+"F12.wireOp",EDGE,"E100.4.1"),sQuery(id+"F12.wireOp",EDGE,"E100.4.2"),sQuery(id+"F12.wireOp",EDGE,"E100.4.3"),sQuery(id+"F12.wireOp",EDGE,"E100.4.4"),sQuery(id+"F12.wireOp",EDGE,"E100.4.5"),sQuery(id+"F12.wireOp",EDGE,"E100.4.6"),sQuery(id+"F12.wireOp",EDGE,"E100.4.7")])],"isStart":false});
            var Q1;
            Q1=makeQuery(id+"F17.opExtrude","CAP_EDGE",EDGE,{"disambiguationData":[OSD([sQuery(id+"F12.wireOp",EDGE,"E100.4.7")])],"isStart":false});
            revolve(context, id + "F20", {"operationType" : NewBodyOperationType.ADD, "entities" : qUnion([Q0]), "axis" : qUnion([Q1]), "revolveType" : RevolveType.ONE_DIRECTION, "angle" : (PI / 4) * radian});
        }
        {
            var Q0;
            Q0=makeQuery(id+"F17.opExtrude","CAP_FACE",FACE,{"disambiguationData":[OSD([sQuery(id+"F12.wireOp",EDGE,"E100.3.0"),sQuery(id+"F12.wireOp",EDGE,"E100.3.1"),sQuery(id+"F12.wireOp",EDGE,"E100.3.2"),sQuery(id+"F12.wireOp",EDGE,"E100.3.3"),sQuery(id+"F12.wireOp",EDGE,"E100.3.4"),sQuery(id+"F12.wireOp",EDGE,"E100.3.5"),sQuery(id+"F12.wireOp",EDGE,"E100.3.6"),sQuery(id+"F12.wireOp",EDGE,"E100.3.7")])],"isStart":false});
            var Q1;
            Q1=makeQuery(id+"F17.opExtrude","CAP_EDGE",EDGE,{"disambiguationData":[OSD([sQuery(id+"F12.wireOp",EDGE,"E100.3.7")])],"isStart":false});
            revolve(context, id + "F21", {"operationType" : NewBodyOperationType.ADD, "entities" : qUnion([Q0]), "axis" : qUnion([Q1]), "revolveType" : RevolveType.ONE_DIRECTION, "angle" : (PI / 4) * radian});
        }
        {
            var Q0;
            Q0=makeQuery(id+"F17.opExtrude","CAP_FACE",FACE,{"disambiguationData":[OSD([sQuery(id+"F12.wireOp",EDGE,"E100.2.0"),sQuery(id+"F12.wireOp",EDGE,"E100.2.1"),sQuery(id+"F12.wireOp",EDGE,"E100.2.2"),sQuery(id+"F12.wireOp",EDGE,"E100.2.3"),sQuery(id+"F12.wireOp",EDGE,"E100.2.4"),sQuery(id+"F12.wireOp",EDGE,"E100.2.5"),sQuery(id+"F12.wireOp",EDGE,"E100.2.6"),sQuery(id+"F12.wireOp",EDGE,"E100.2.7")])],"isStart":false});
            var Q1;
            Q1=makeQuery(id+"F17.opExtrude","CAP_EDGE",EDGE,{"disambiguationData":[OSD([sQuery(id+"F12.wireOp",EDGE,"E100.2.7")])],"isStart":false});
            revolve(context, id + "F22", {"operationType" : NewBodyOperationType.ADD, "entities" : qUnion([Q0]), "axis" : qUnion([Q1]), "revolveType" : RevolveType.ONE_DIRECTION, "angle" : (PI / 4) * radian});
        }
        {
            var Q0;
            {var subQ0=sQuery(id+"F12.wireOp",EDGE,"E83.cCircle");var subQ1=sQuery(id+"F12.wireOp",EDGE,"E76");var subQ2=makeQuery(id+"F12.imprint","INTERSECT",VERTEX,{"disambiguationData":[OD(0.0)],"derivedFrom":[subQ1,subQ0]});Q0=makeQuery(id+"F12.imprint","IMPRINT",FACE,{"disambiguationData":[TD([[makeQuery(id+"F12.imprint","IMPRINT",EDGE,{"disambiguationData":[TD([[subQ2,-1.0]])],"derivedFrom":subQ1}),1.0]])]});}
            var Q1;
            {var subQ1=sQuery(id+"F12.wireOp",EDGE,"E97");var subQ3=sQuery(id+"F12.wireOp",EDGE,"E76");var subQ4=makeQuery(id+"F12.imprint","INTERSECT",VERTEX,{"derivedFrom":[subQ3,subQ1]});Q1=makeQuery(id+"F12.imprint","IMPRINT",FACE,{"disambiguationData":[TD([[makeQuery(id+"F12.imprint","IMPRINT",EDGE,{"disambiguationData":[TD([[subQ4,-1.0]])],"derivedFrom":subQ3}),1.0]])]});}
            var Q2;
            {var subQ0=sQuery(id+"F12.wireOp",EDGE,"E94.4.8");var subQ1=sQuery(id+"F12.wireOp",EDGE,"E83.cCircle");var subQ2=makeQuery(id+"F12.imprint","INTERSECT",VERTEX,{"derivedFrom":[subQ1,subQ0]});Q2=makeQuery(id+"F12.imprint","IMPRINT",FACE,{"disambiguationData":[TD([[makeQuery(id+"F12.imprint","IMPRINT",EDGE,{"disambiguationData":[TD([[subQ2,1.0]])],"derivedFrom":subQ1}),-1.0]])]});}
            var Q3;
            {var subQ0=sQuery(id+"F12.wireOp",EDGE,"E94.3.8");var subQ1=sQuery(id+"F12.wireOp",EDGE,"E83.cCircle");var subQ2=makeQuery(id+"F12.imprint","INTERSECT",VERTEX,{"derivedFrom":[subQ1,subQ0]});Q3=makeQuery(id+"F12.imprint","IMPRINT",FACE,{"disambiguationData":[TD([[makeQuery(id+"F12.imprint","IMPRINT",EDGE,{"disambiguationData":[TD([[subQ2,-1.0]])],"derivedFrom":subQ1}),-1.0]])]});}
            var Q4;
            {var subQ0=sQuery(id+"F12.wireOp",EDGE,"E94.1.8");var subQ1=sQuery(id+"F12.wireOp",EDGE,"E83.cCircle");var subQ2=makeQuery(id+"F12.imprint","INTERSECT",VERTEX,{"derivedFrom":[subQ1,subQ0]});Q4=makeQuery(id+"F12.imprint","IMPRINT",FACE,{"disambiguationData":[TD([[makeQuery(id+"F12.imprint","IMPRINT",EDGE,{"disambiguationData":[TD([[subQ2,-1.0]])],"derivedFrom":subQ1}),-1.0]])]});}
            var Q5;
            {var subQ0=sQuery(id+"F12.wireOp",EDGE,"E83.7");var subQ1=sQuery(id+"F12.wireOp",EDGE,"E83.cCircle");var subQ2=makeQuery(id+"F12.imprint","INTERSECT",VERTEX,{"derivedFrom":[subQ1,subQ0]});Q5=makeQuery(id+"F12.imprint","IMPRINT",FACE,{"disambiguationData":[TD([[makeQuery(id+"F12.imprint","IMPRINT",EDGE,{"disambiguationData":[TD([[subQ2,-1.0]])],"derivedFrom":subQ1}),-1.0]])]});}
            var Q6;
            {var subQ0=sQuery(id+"F12.wireOp",EDGE,"E83.1");var subQ1=sQuery(id+"F12.wireOp",EDGE,"E76");var subQ2=makeQuery(id+"F12.imprint","INTERSECT",VERTEX,{"derivedFrom":[subQ1,subQ0]});Q6=makeQuery(id+"F12.imprint","IMPRINT",FACE,{"disambiguationData":[TD([[makeQuery(id+"F12.imprint","IMPRINT",EDGE,{"disambiguationData":[TD([[subQ2,-1.0]])],"derivedFrom":subQ1}),-1.0]])]});}
            var Q7;
            {var subQ0=sQuery(id+"F12.wireOp",EDGE,"E83.cCircle");var subQ1=sQuery(id+"F12.wireOp",EDGE,"E77");var subQ2=makeQuery(id+"F12.imprint","INTERSECT",VERTEX,{"disambiguationData":[OD(1.0)],"derivedFrom":[subQ1,subQ0]});Q7=makeQuery(id+"F12.imprint","IMPRINT",FACE,{"disambiguationData":[TD([[makeQuery(id+"F12.imprint","IMPRINT",EDGE,{"disambiguationData":[TD([[subQ2,-1.0]])],"derivedFrom":subQ1}),1.0]])]});}
            var Q8;
            {var subQ14=sQuery(id+"F12.wireOp",EDGE,"E96");Q8=makeQuery(id+"F12.imprint","IMPRINT",FACE,{"disambiguationData":[TD([[makeQuery(id+"F12.imprint","IMPRINT",EDGE,{"derivedFrom":subQ14}),1.0]])]});}
            var Q9;
            {var subQ1=sQuery(id+"F12.wireOp",EDGE,"E76");var subQ5=sQuery(id+"F12.wireOp",EDGE,"E83.cCircle");var subQ6=makeQuery(id+"F12.imprint","INTERSECT",VERTEX,{"disambiguationData":[OD(1.0)],"derivedFrom":[subQ1,subQ5]});Q9=makeQuery(id+"F12.imprint","IMPRINT",FACE,{"disambiguationData":[TD([[makeQuery(id+"F12.imprint","IMPRINT",EDGE,{"disambiguationData":[TD([[subQ6,-1.0]])],"derivedFrom":subQ1}),1.0]])]});}
            var Q10;
            {var subQ16=sQuery(id+"F12.wireOp",EDGE,"E100.3.1");Q10=makeQuery(id+"F12.imprint","IMPRINT",FACE,{"disambiguationData":[TD([[makeQuery(id+"F12.imprint","IMPRINT",EDGE,{"derivedFrom":subQ16}),-1.0]])]});}
            var Q11;
            {var subQ0=sQuery(id+"F12.wireOp",EDGE,"E83.cCircle");var subQ1=sQuery(id+"F12.wireOp",EDGE,"E76");var subQ2=makeQuery(id+"F12.imprint","INTERSECT",VERTEX,{"disambiguationData":[OD(1.0)],"derivedFrom":[subQ1,subQ0]});Q11=makeQuery(id+"F12.imprint","IMPRINT",FACE,{"disambiguationData":[TD([[makeQuery(id+"F12.imprint","IMPRINT",EDGE,{"disambiguationData":[TD([[subQ2,-1.0]])],"derivedFrom":subQ1}),-1.0]])]});}
            var Q12;
            {var subQ0=sQuery(id+"F12.wireOp",EDGE,"E94.5.8");var subQ1=sQuery(id+"F12.wireOp",EDGE,"E83.cCircle");var subQ2=makeQuery(id+"F12.imprint","INTERSECT",VERTEX,{"derivedFrom":[subQ1,subQ0]});Q12=makeQuery(id+"F12.imprint","IMPRINT",FACE,{"disambiguationData":[TD([[makeQuery(id+"F12.imprint","IMPRINT",EDGE,{"disambiguationData":[TD([[subQ2,-1.0]])],"derivedFrom":subQ1}),-1.0]])]});}
            var Q13;
            {var subQ0=sQuery(id+"F12.wireOp",EDGE,"E83.6");var subQ1=sQuery(id+"F12.wireOp",EDGE,"E83.5");var subQ2=makeQuery(id+"F12.imprint","INTERSECT",VERTEX,{"derivedFrom":[subQ1,subQ0]});Q13=makeQuery(id+"F12.imprint","IMPRINT",FACE,{"disambiguationData":[TD([[makeQuery(id+"F12.imprint","IMPRINT",EDGE,{"disambiguationData":[TD([[subQ2,1.0]])],"derivedFrom":subQ1}),-1.0]])]});}
            var Q14;
            {var subQ0=sQuery(id+"F12.wireOp",EDGE,"E109.MirrorCS");Q14=makeQuery(id+"F12.imprint","IMPRINT",FACE,{"disambiguationData":[TD([[makeQuery(id+"F12.imprint","IMPRINT",EDGE,{"derivedFrom":subQ0}),1.0]])]});}
            var Q15;
            {var subQ1=sQuery(id+"F12.wireOp",EDGE,"E105");var subQ3=sQuery(id+"F12.wireOp",EDGE,"E76");var subQ4=makeQuery(id+"F12.imprint","INTERSECT",VERTEX,{"derivedFrom":[subQ3,subQ1]});Q15=makeQuery(id+"F12.imprint","IMPRINT",FACE,{"disambiguationData":[TD([[makeQuery(id+"F12.imprint","IMPRINT",EDGE,{"disambiguationData":[TD([[subQ4,-1.0]])],"derivedFrom":subQ3}),1.0]])]});}
            var Q16;
            {var subQ5=sQuery(id+"F12.wireOp",EDGE,"E106.MirrorCS");Q16=makeQuery(id+"F12.imprint","IMPRINT",FACE,{"disambiguationData":[TD([[makeQuery(id+"F12.imprint","IMPRINT",EDGE,{"derivedFrom":subQ5}),-1.0]])]});}
            var Q17;
            {var subQ5=sQuery(id+"F12.wireOp",EDGE,"E106.MirrorCS");Q17=makeQuery(id+"F12.imprint","IMPRINT",FACE,{"disambiguationData":[TD([[makeQuery(id+"F12.imprint","IMPRINT",EDGE,{"derivedFrom":subQ5}),1.0]])]});}
            var Q18;
            {var subQ0=sQuery(id+"F12.wireOp",EDGE,"E107");var subQ1=sQuery(id+"F12.wireOp",EDGE,"E77");var subQ2=makeQuery(id+"F12.imprint","INTERSECT",VERTEX,{"derivedFrom":[subQ1,subQ0]});Q18=makeQuery(id+"F12.imprint","IMPRINT",FACE,{"disambiguationData":[TD([[makeQuery(id+"F12.imprint","IMPRINT",EDGE,{"disambiguationData":[TD([[subQ2,-1.0]])],"derivedFrom":subQ1}),1.0]])]});}
            var Q19;
            {var subQ5=sQuery(id+"F12.wireOp",EDGE,"E109.MirrorCS");Q19=makeQuery(id+"F12.imprint","IMPRINT",FACE,{"disambiguationData":[TD([[makeQuery(id+"F12.imprint","IMPRINT",EDGE,{"derivedFrom":subQ5}),-1.0]])]});}
            extrude(context, id + "F23", {"entities" : qUnion([Q0, Q1, Q2, Q3, Q4, Q5, Q6, Q7, Q8, Q9, Q10, Q11, Q12, Q13, Q14, Q15, Q16, Q17, Q18, Q19]), "operationType" : NewBodyOperationType.ADD, "depth" : 1.25 * mm});
        }
        {
            var Q0;
            {var subQ0=sQuery(id+"F12.wireOp",EDGE,"E100.2.7");var subQ1=makeQuery(id+"F17.opExtrude","SWEPT_FACE",FACE,{"disambiguationData":[OSD([subQ0])]});var subQ3=sQuery(id+"F4.wireOp",EDGE,"E60.bottom");var subQ4=makeQuery(id+"F13.opExtrude","CAP_EDGE",EDGE,{"disambiguationData":[OSD([subQ3])],"isStart":false});var subQ6=sQuery(id+"F4.wireOp",EDGE,"E60.top");var subQ15=sQuery(id+"F12.wireOp",EDGE,"E76");var subQ30=sQuery(id+"F12.wireOp",EDGE,"E95.3");var subQ32=sQuery(id+"F12.wireOp",EDGE,"E77");var subQ33=sQuery(id+"F12.wireOp",EDGE,"E83.cCircle");var subQ41=sQuery(id+"F12.wireOp",EDGE,"E94.2.8");var subQ61=sQuery(id+"F12.wireOp",EDGE,"E100.2.6");Q0=makeQuery(id+"F23.boolean.opBoolean","SPLIT",FACE,{"disambiguationData":[TD([subQ1])],"derivedFrom":makeQuery(id+"F17.boolean.opBoolean","SPLIT",FACE,{"disambiguationData":[TD([makeQuery(id+"F13.opExtrude","SWEPT_FACE",FACE,{"disambiguationData":[OSD([subQ33])]})])],"derivedFrom":makeQuery(id+"F15.boolean.opBoolean","MERGE",FACE,{"derivedFrom":[makeQuery(id+"F13.opExtrude","CAP_FACE",FACE,{"disambiguationData":[OSD([subQ3,subQ6,subQ15,subQ32,subQ33,subQ41,subQ30,subQ61])],"isStart":false}),makeQuery(id+"F15.opExtrude","SWEPT_FACE",FACE,{"disambiguationData":[OSD([subQ3]),TDD([makeQuery(id+"F14.imprint","IMPRINT",EDGE,{"derivedFrom":subQ4})])]})]})})});}
            var Q1;
            {var subQ1=sQuery(id+"F4.wireOp",EDGE,"E60.bottom");var subQ3=sQuery(id+"F4.wireOp",EDGE,"E60.top");var subQ4=makeQuery(id+"F5.opExtrude","CAP_EDGE",EDGE,{"disambiguationData":[OSD([subQ3])],"isStart":false});var subQ7=sQuery(id+"F4.wireOp",EDGE,"E60.right");var subQ8=sQuery(id+"F4.wireOp",EDGE,"E60.left");var subQ9=makeQuery(id+"F5.opExtrude","CAP_FACE",FACE,{"disambiguationData":[OSD([subQ1,subQ3,subQ8,subQ7])],"isStart":false});var subQ10=makeQuery(id+"F5.opExtrude","SWEPT_FACE",FACE,{"disambiguationData":[OSD([subQ7])]});var subQ15=makeQuery(id+"F5.opExtrude","SWEPT_FACE",FACE,{"disambiguationData":[OSD([subQ1])]});var subQ18=makeQuery(id+"F7.opExtrude","SWEPT_FACE",FACE,{"disambiguationData":[OSD([subQ3]),TDD([makeQuery(id+"F6.imprint","IMPRINT",EDGE,{"disambiguationData":[TD([[makeQuery(id+"F6.imprint","INTERSECT",VERTEX,{"derivedFrom":[subQ4,sQuery(id+"F6.wireOp",EDGE,"E70")]}),-1.0]])],"derivedFrom":subQ4})])]});Q1=makeQuery(id+"F23.boolean.opBoolean","SPLIT",FACE,{"disambiguationData":[TD([makeQuery(id+"F23.opExtrude","SWEPT_FACE",FACE,{"disambiguationData":[OSD([sQuery(id+"F12.wireOp",EDGE,"E104")])]})])],"derivedFrom":makeQuery(id+"F17.boolean.opBoolean","SPLIT",FACE,{"disambiguationData":[TD([subQ15])],"derivedFrom":makeQuery(id+"F16.boolean.opBoolean","SPLIT",FACE,{"disambiguationData":[TD([subQ15])],"derivedFrom":makeQuery(id+"F13.boolean.opBoolean","SPLIT",FACE,{"disambiguationData":[TD([subQ10])],"derivedFrom":makeQuery(id+"F7.boolean.opBoolean","MERGE",FACE,{"derivedFrom":[subQ9,subQ18]})})})})});}
            var Q2;
            Q2=makeQuery(id+"F23.opExtrude","CAP_FACE",FACE,{"disambiguationData":[OSD([sQuery(id+"F12.wireOp",EDGE,"E76"),sQuery(id+"F12.wireOp",EDGE,"E77"),sQuery(id+"F12.wireOp",EDGE,"E83.cCircle"),sQuery(id+"F12.wireOp",EDGE,"E83.1"),sQuery(id+"F12.wireOp",EDGE,"E83.3"),sQuery(id+"F12.wireOp",EDGE,"E83.5"),sQuery(id+"F12.wireOp",EDGE,"E83.6"),sQuery(id+"F12.wireOp",EDGE,"E83.7"),sQuery(id+"F12.wireOp",EDGE,"E94.1.8"),sQuery(id+"F12.wireOp",EDGE,"E94.3.8"),sQuery(id+"F12.wireOp",EDGE,"E94.4.8"),sQuery(id+"F12.wireOp",EDGE,"E94.5.8"),sQuery(id+"F12.wireOp",EDGE,"E94.6.8"),sQuery(id+"F12.wireOp",EDGE,"E95.3"),sQuery(id+"F12.wireOp",EDGE,"E95.7"),sQuery(id+"F12.wireOp",EDGE,"E96"),sQuery(id+"F12.wireOp",EDGE,"E97"),sQuery(id+"F12.wireOp",EDGE,"E98"),sQuery(id+"F12.wireOp",EDGE,"E100.1.1"),sQuery(id+"F12.wireOp",EDGE,"E100.1.3"),sQuery(id+"F12.wireOp",EDGE,"E100.1.4"),sQuery(id+"F12.wireOp",EDGE,"E100.1.7"),sQuery(id+"F12.wireOp",EDGE,"E100.2.1"),sQuery(id+"F12.wireOp",EDGE,"E100.2.3"),sQuery(id+"F12.wireOp",EDGE,"E100.2.4"),sQuery(id+"F12.wireOp",EDGE,"E100.2.7"),sQuery(id+"F12.wireOp",EDGE,"E100.3.1"),sQuery(id+"F12.wireOp",EDGE,"E100.3.3"),sQuery(id+"F12.wireOp",EDGE,"E100.3.4"),sQuery(id+"F12.wireOp",EDGE,"E100.3.7"),sQuery(id+"F12.wireOp",EDGE,"E100.4.1"),sQuery(id+"F12.wireOp",EDGE,"E100.4.3"),sQuery(id+"F12.wireOp",EDGE,"E100.4.4"),sQuery(id+"F12.wireOp",EDGE,"E100.4.7"),sQuery(id+"F12.wireOp",EDGE,"E104"),sQuery(id+"F12.wireOp",EDGE,"E105"),sQuery(id+"F12.wireOp",EDGE,"E110")])],"isStart":false});
            extrude(context, id + "F24", {"entities" : qUnion([Q0, Q1]), "operationType" : NewBodyOperationType.ADD, "endBound" : BoundingType.UP_TO_SURFACE, "endBoundEntityFace" : qUnion([Q2]), "depth" : 25 * mm});
        }
        {
            var Q0;
            Q0=makeQuery(id+"F1.opRevolve","SWEPT_BODY",BODY,{"disambiguationData":[OSD([sQuery(id+"F0.wireOp",EDGE,"E7"),sQuery(id+"F0.wireOp",EDGE,"E8"),sQuery(id+"F0.wireOp",EDGE,"E10.MirrorCS"),sQuery(id+"F0.wireOp",EDGE,"E31.1.endCap"),sQuery(id+"F0.wireOp",EDGE,"E31.1.left"),sQuery(id+"F0.wireOp",EDGE,"E31.1.right"),sQuery(id+"F0.wireOp",EDGE,"E31.2.startCap"),sQuery(id+"F0.wireOp",EDGE,"E31.2.endCap"),sQuery(id+"F0.wireOp",EDGE,"E31.2.left"),sQuery(id+"F0.wireOp",EDGE,"E31.2.right"),sQuery(id+"F0.wireOp",EDGE,"E38"),sQuery(id+"F0.wireOp",EDGE,"E39"),sQuery(id+"F0.wireOp",EDGE,"E41"),sQuery(id+"F0.wireOp",EDGE,"E45.0.startCap"),sQuery(id+"F0.wireOp",EDGE,"E45.0.left"),sQuery(id+"F0.wireOp",EDGE,"E45.0.right"),sQuery(id+"F0.wireOp",EDGE,"E45.1.startCap"),sQuery(id+"F0.wireOp",EDGE,"E45.1.endCap"),sQuery(id+"F0.wireOp",EDGE,"E45.1.left"),sQuery(id+"F0.wireOp",EDGE,"E45.1.right"),sQuery(id+"F0.wireOp",EDGE,"E47.MirrorCS"),sQuery(id+"F0.wireOp",EDGE,"E49.MirrorCS"),sQuery(id+"F0.wireOp",EDGE,"E50.MirrorCS"),sQuery(id+"F0.wireOp",EDGE,"E52.MirrorCS"),sQuery(id+"F0.wireOp",EDGE,"E53.MirrorCS"),sQuery(id+"F0.wireOp",EDGE,"E55.MirrorCS"),sQuery(id+"F0.wireOp",EDGE,"E56.MirrorCS"),sQuery(id+"F0.wireOp",EDGE,"E59.0.endCap"),sQuery(id+"F0.wireOp",EDGE,"E59.0.left"),sQuery(id+"F0.wireOp",EDGE,"E59.0.right"),sQuery(id+"F0.wireOp",EDGE,"E59.1.startCap"),sQuery(id+"F0.wireOp",EDGE,"E59.1.endCap"),sQuery(id+"F0.wireOp",EDGE,"E59.1.left"),sQuery(id+"F0.wireOp",EDGE,"E59.1.right")])]});
            var Q1;
            Q1=makeQuery(id+"F2.opExtrude","CAP_VERTEX",VERTEX,{"disambiguationData":[OSD([sQuery(id+"F0.wireOp",EDGE,"E8"),sQuery(id+"F0.wireOp",EDGE,"E10.MirrorCS")])],"isStart":false});
            transform(context, id + "F25", {"entities" : qUnion([Q0]), "transformType" : TransformType.SCALE_UNIFORMLY, "scale" : 1.6, "scalePoint" : qUnion([Q1]), "makeCopy" : false});
        }
        {
            var Q0;
            Q0=makeQuery(id+"F5.opExtrude","SWEPT_BODY",BODY,{"disambiguationData":[OSD([sQuery(id+"F4.wireOp",EDGE,"E60.bottom"),sQuery(id+"F4.wireOp",EDGE,"E60.top"),sQuery(id+"F4.wireOp",EDGE,"E60.left"),sQuery(id+"F4.wireOp",EDGE,"E60.right")])]});
            var Q1;
            Q1=makeQuery(id+"F5.opExtrude","CAP_VERTEX",VERTEX,{"disambiguationData":[OSD([sQuery(id+"F4.wireOp",EDGE,"E60.top"),sQuery(id+"F4.wireOp",EDGE,"E60.left")])],"isStart":true});
            transform(context, id + "F26", {"entities" : qUnion([Q0]), "transformType" : TransformType.SCALE_UNIFORMLY, "scale" : 1.75, "scalePoint" : qUnion([Q1]), "makeCopy" : false});
        }
    });
